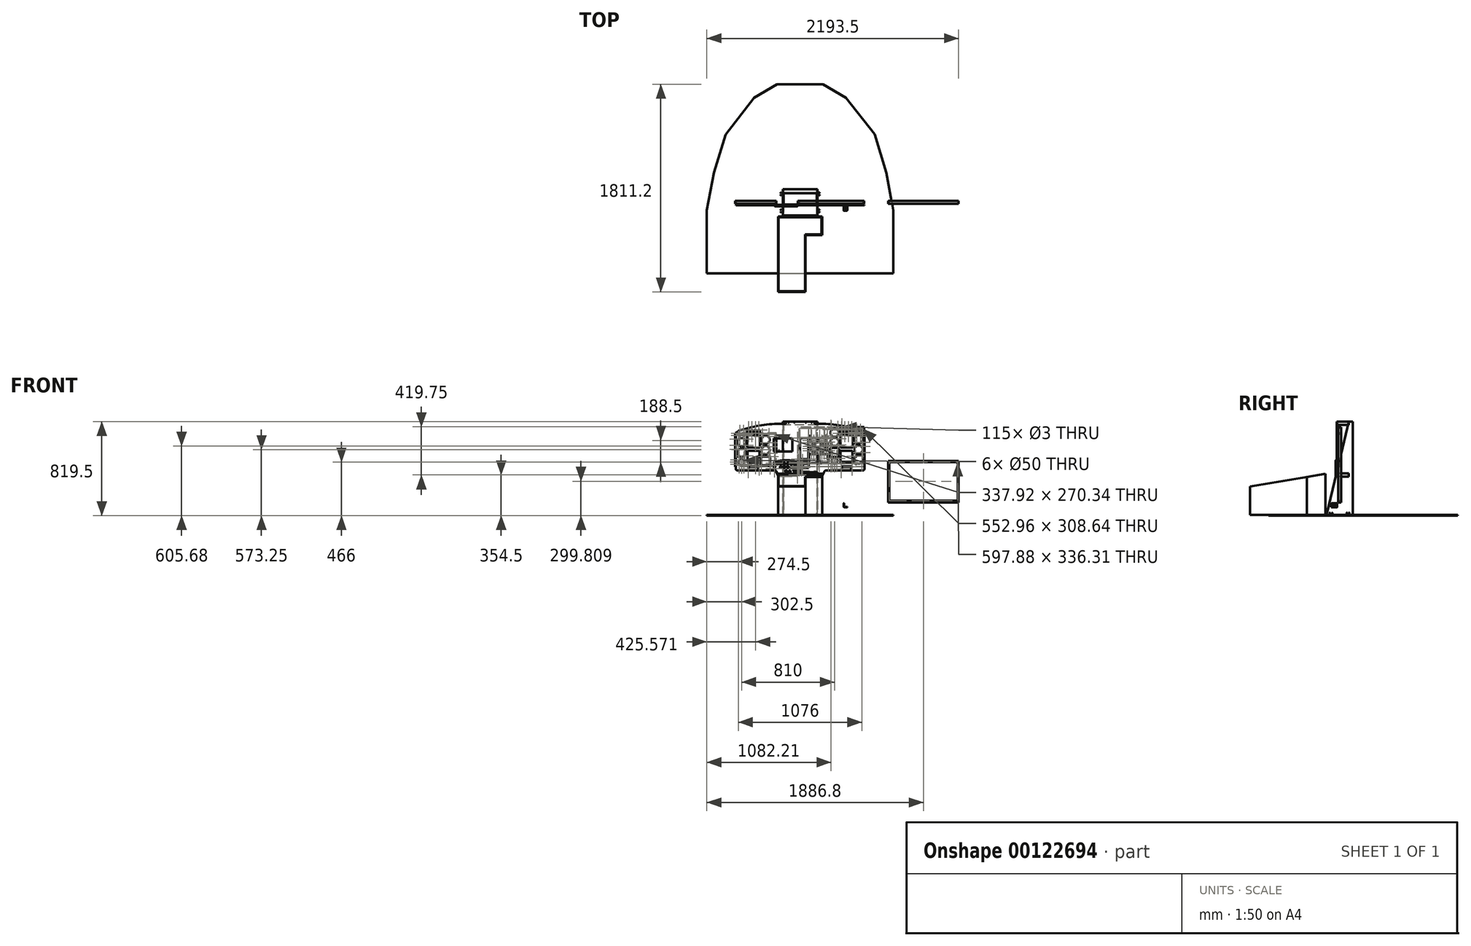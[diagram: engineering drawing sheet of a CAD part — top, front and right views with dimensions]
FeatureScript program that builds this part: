
annotation { "Feature Type Name" : "Feature", "Feature Type Description" : "" }
export const myFeature = defineFeature(function(context is Context, id is Id, definition is map)
    precondition{}
    {
        {
            var Q0;
            Q0=qCreatedBy(makeId("Front.planeOp"),FACE);
            var sketch = newSketch(context, id + "F0", { "sketchPlane" : qUnion([Q0])});
            skLineSegment(sketch, "E0", {"start": v(0, 0) * mm, "end": v(-185, 0) * mm});
            skLineSegment(sketch, "E1", {"start": v(-233, 55.5) * mm, "end": v(-550.5, 55.5) * mm});
            skLineSegment(sketch, "E2", {"start": v(-560, 65) * mm, "end": v(-560, 360) * mm});
            skLineSegment(sketch, "E3", {"start": v(-178, 460) * mm, "end": v(0, 460) * mm});
            skArc(sketch, "E4", {"start": v(-207, 39) * mm, "mid": v(-217.57, 51.08) * mm, "end": v(-233, 55.5) * mm});
            skArc(sketch, "E5", {"start": v(-193, 5.6) * mm, "mid": v(-189.73, 1.76) * mm, "end": v(-185, 0) * mm});
            skLineSegment(sketch, "E6", {"start": v(-207, 39) * mm, "end": v(-193, 5.6) * mm});
            skArc(sketch, "E7", {"start": v(-560, 65) * mm, "mid": v(-557.22, 58.28) * mm, "end": v(-550.5, 55.5) * mm});
            skArc(sketch, "E8", {"start": v(-533, 400) * mm, "mid": v(-552.32, 383.93) * mm, "end": v(-560, 360) * mm});
            skArc(sketch, "E9", {"start": v(-178, 460) * mm, "mid": v(-358.02, 444.9) * mm, "end": v(-533, 400) * mm});
            skArc(sketch, "E10.MirrorCS", {"start": v(193, 5.6) * mm, "mid": v(189.73, 1.76) * mm, "end": v(185, 0) * mm});
            skLineSegment(sketch, "E11.MirrorCS", {"start": v(207, 39) * mm, "end": v(193, 5.6) * mm});
            skArc(sketch, "E12.MirrorCS", {"start": v(560, 65) * mm, "mid": v(557.22, 58.28) * mm, "end": v(550.5, 55.5) * mm});
            skArc(sketch, "E13.MirrorCS", {"start": v(207, 39) * mm, "mid": v(217.57, 51.08) * mm, "end": v(233, 55.5) * mm});
            skArc(sketch, "E14.MirrorCS", {"start": v(533, 400) * mm, "mid": v(552.32, 383.93) * mm, "end": v(560, 360) * mm});
            skArc(sketch, "E15.MirrorCS", {"start": v(178, 460) * mm, "mid": v(358.02, 444.9) * mm, "end": v(533, 400) * mm});
            skLineSegment(sketch, "E16.MirrorCS", {"start": v(178, 460) * mm, "end": v(0, 460) * mm});
            skLineSegment(sketch, "E17.MirrorCS", {"start": v(0, 0) * mm, "end": v(185, 0) * mm});
            skLineSegment(sketch, "E18.MirrorCS", {"start": v(233, 55.5) * mm, "end": v(550.5, 55.5) * mm});
            skLineSegment(sketch, "E19.MirrorCS", {"start": v(560, 65) * mm, "end": v(560, 360) * mm});
            skLineSegment(sketch, "E20.bottom", {"start": v(-125, 460) * mm, "end": v(125, 460) * mm});
            skLineSegment(sketch, "E20.top", {"start": v(-125, 480) * mm, "end": v(125, 480) * mm});
            skLineSegment(sketch, "E20.left", {"start": v(-125, 460) * mm, "end": v(-125, 480) * mm});
            skLineSegment(sketch, "E20.right", {"start": v(125, 460) * mm, "end": v(125, 480) * mm});
            skPoint(sketch, "E20.middle", {"position": v(0, 470) * mm});
            skSolve(sketch);
        }
        {
            var Q0;
            Q0=qSketchRegion(id+"F0",true);
            extrude(context, id + "F1", {"entities" : qUnion([Q0]), "depth" : 3 * mm});
        }
        {
            var Q0;
            Q0=makeQuery(id+"F1.opExtrude","CAP_FACE",FACE,{"disambiguationData":[OSD([sQuery(id+"F0.wireOp",EDGE,"E0"),sQuery(id+"F0.wireOp",EDGE,"E1"),sQuery(id+"F0.wireOp",EDGE,"E2"),sQuery(id+"F0.wireOp",EDGE,"E3"),sQuery(id+"F0.wireOp",EDGE,"E4"),sQuery(id+"F0.wireOp",EDGE,"E5"),sQuery(id+"F0.wireOp",EDGE,"E6"),sQuery(id+"F0.wireOp",EDGE,"E7"),sQuery(id+"F0.wireOp",EDGE,"E8"),sQuery(id+"F0.wireOp",EDGE,"E9"),sQuery(id+"F0.wireOp",EDGE,"E10.MirrorCS"),sQuery(id+"F0.wireOp",EDGE,"E11.MirrorCS"),sQuery(id+"F0.wireOp",EDGE,"E12.MirrorCS"),sQuery(id+"F0.wireOp",EDGE,"E13.MirrorCS"),sQuery(id+"F0.wireOp",EDGE,"E14.MirrorCS"),sQuery(id+"F0.wireOp",EDGE,"E15.MirrorCS"),sQuery(id+"F0.wireOp",EDGE,"E16.MirrorCS"),sQuery(id+"F0.wireOp",EDGE,"E17.MirrorCS"),sQuery(id+"F0.wireOp",EDGE,"E18.MirrorCS"),sQuery(id+"F0.wireOp",EDGE,"E19.MirrorCS")])],"isStart":false});
            var sketch = newSketch(context, id + "F2", { "sketchPlane" : qUnion([Q0])});
            skCircle(sketch, "E21", {"center": v(-510, 300) * mm, "radius": 35 * mm});
            skCircle(sketch, "E22", {"center": v(-510, 210) * mm, "radius": 35 * mm});
            skCircle(sketch, "E23", {"center": v(-510, 126.5) * mm, "radius": 25 * mm});
            skCircle(sketch, "E24", {"center": v(-300, 322) * mm, "radius": 35 * mm});
            skCircle(sketch, "E25", {"center": v(-300, 232) * mm, "radius": 35 * mm});
            skCircle(sketch, "E26", {"center": v(510, 237) * mm, "radius": 35 * mm});
            skCircle(sketch, "E27", {"center": v(510, 325) * mm, "radius": 35 * mm});
            skCircle(sketch, "E28", {"center": v(-538, 328) * mm, "radius": 1.5 * mm});
            skCircle(sketch, "E29", {"center": v(-538, 272) * mm, "radius": 1.5 * mm});
            skCircle(sketch, "E30", {"center": v(-482, 328) * mm, "radius": 1.5 * mm});
            skCircle(sketch, "E31", {"center": v(-482, 272) * mm, "radius": 1.5 * mm});
            skCircle(sketch, "E32", {"center": v(-538, 238) * mm, "radius": 1.5 * mm});
            skCircle(sketch, "E33", {"center": v(-538, 182) * mm, "radius": 1.5 * mm});
            skCircle(sketch, "E34", {"center": v(-482, 238) * mm, "radius": 1.5 * mm});
            skCircle(sketch, "E35", {"center": v(-482, 182) * mm, "radius": 1.5 * mm});
            skCircle(sketch, "E36", {"center": v(-328, 350) * mm, "radius": 1.5 * mm});
            skCircle(sketch, "E37", {"center": v(-272, 350) * mm, "radius": 1.5 * mm});
            skCircle(sketch, "E38", {"center": v(-272, 294) * mm, "radius": 1.5 * mm});
            skCircle(sketch, "E39", {"center": v(-328, 260) * mm, "radius": 1.5 * mm});
            skCircle(sketch, "E40", {"center": v(-272, 260) * mm, "radius": 1.5 * mm});
            skCircle(sketch, "E41", {"center": v(-272, 204) * mm, "radius": 1.5 * mm});
            skLineSegment(sketch, "E42.bottom", {"start": v(-350, 252.75) * mm, "end": v(-460, 252.75) * mm});
            skLineSegment(sketch, "E42.top", {"start": v(-350, 362.75) * mm, "end": v(-460, 362.75) * mm});
            skLineSegment(sketch, "E42.left", {"start": v(-350, 252.75) * mm, "end": v(-350, 362.75) * mm});
            skLineSegment(sketch, "E42.right", {"start": v(-460, 252.75) * mm, "end": v(-460, 362.75) * mm});
            skPoint(sketch, "E42.middle", {"position": v(-405, 307.75) * mm});
            skLineSegment(sketch, "E43.bottom", {"start": v(-352.5, 121) * mm, "end": v(-457.5, 121) * mm});
            skLineSegment(sketch, "E43.top", {"start": v(-352.5, 226) * mm, "end": v(-457.5, 226) * mm});
            skLineSegment(sketch, "E43.left", {"start": v(-352.5, 121) * mm, "end": v(-352.5, 226) * mm});
            skLineSegment(sketch, "E43.right", {"start": v(-457.5, 121) * mm, "end": v(-457.5, 226) * mm});
            skPoint(sketch, "E43.middle", {"position": v(-405, 173.5) * mm});
            skCircle(sketch, "E44", {"center": v(-530, 146.5) * mm, "radius": 1.5 * mm});
            skCircle(sketch, "E45", {"center": v(-530, 106.5) * mm, "radius": 1.5 * mm});
            skCircle(sketch, "E46", {"center": v(-490, 146.5) * mm, "radius": 1.5 * mm});
            skCircle(sketch, "E47", {"center": v(-490, 106.5) * mm, "radius": 1.5 * mm});
            skLineSegment(sketch, "E48.bottom", {"start": v(-362.5, 61.5) * mm, "end": v(-447.5, 61.5) * mm});
            skLineSegment(sketch, "E48.top", {"start": v(-362.5, 89.5) * mm, "end": v(-447.5, 89.5) * mm});
            skLineSegment(sketch, "E48.left", {"start": v(-362.5, 61.5) * mm, "end": v(-362.5, 89.5) * mm});
            skLineSegment(sketch, "E48.right", {"start": v(-447.5, 61.5) * mm, "end": v(-447.5, 89.5) * mm});
            skPoint(sketch, "E48.middle", {"position": v(-405, 75.5) * mm});
            skCircle(sketch, "E49", {"center": v(510, 149) * mm, "radius": 35 * mm});
            skCircle(sketch, "E50", {"center": v(300, 383) * mm, "radius": 35 * mm});
            skCircle(sketch, "E51", {"center": v(300, 303) * mm, "radius": 35 * mm});
            skCircle(sketch, "E52", {"center": v(300, 138) * mm, "radius": 25 * mm});
            skLineSegment(sketch, "E53.0", {"start": v(-260, 165.5) * mm, "end": v(-260, 105.5) * mm});
            skLineSegment(sketch, "E53.1", {"start": v(-260, 105.5) * mm, "end": v(-270, 95.5) * mm});
            skLineSegment(sketch, "E53.2", {"start": v(-270, 95.5) * mm, "end": v(-330, 95.5) * mm});
            skLineSegment(sketch, "E53.3", {"start": v(-330, 95.5) * mm, "end": v(-340, 105.5) * mm});
            skLineSegment(sketch, "E53.4", {"start": v(-340, 105.5) * mm, "end": v(-340, 165.5) * mm});
            skLineSegment(sketch, "E53.5", {"start": v(-340, 165.5) * mm, "end": v(-330, 175.5) * mm});
            skLineSegment(sketch, "E53.6", {"start": v(-330, 175.5) * mm, "end": v(-270, 175.5) * mm});
            skLineSegment(sketch, "E53.7", {"start": v(-270, 175.5) * mm, "end": v(-260, 165.5) * mm});
            skPoint(sketch, "E54", {"position": v(-300, 135.5) * mm});
            skLineSegment(sketch, "E55.bottom", {"start": v(350, 362.75) * mm, "end": v(460, 362.75) * mm});
            skLineSegment(sketch, "E55.top", {"start": v(350, 252.75) * mm, "end": v(460, 252.75) * mm});
            skLineSegment(sketch, "E55.left", {"start": v(350, 362.75) * mm, "end": v(350, 252.75) * mm});
            skLineSegment(sketch, "E55.right", {"start": v(460, 362.75) * mm, "end": v(460, 252.75) * mm});
            skPoint(sketch, "E55.middle", {"position": v(405, 307.75) * mm});
            skLineSegment(sketch, "E56.bottom", {"start": v(352.5, 226) * mm, "end": v(457.5, 226) * mm});
            skLineSegment(sketch, "E56.top", {"start": v(352.5, 121) * mm, "end": v(457.5, 121) * mm});
            skLineSegment(sketch, "E56.left", {"start": v(352.5, 226) * mm, "end": v(352.5, 121) * mm});
            skLineSegment(sketch, "E56.right", {"start": v(457.5, 226) * mm, "end": v(457.5, 121) * mm});
            skPoint(sketch, "E56.middle", {"position": v(405, 173.5) * mm});
            skLineSegment(sketch, "E57.bottom", {"start": v(362.5, 89.5) * mm, "end": v(447.5, 89.5) * mm});
            skLineSegment(sketch, "E57.top", {"start": v(362.5, 61.5) * mm, "end": v(447.5, 61.5) * mm});
            skLineSegment(sketch, "E57.left", {"start": v(362.5, 89.5) * mm, "end": v(362.5, 61.5) * mm});
            skLineSegment(sketch, "E57.right", {"start": v(447.5, 89.5) * mm, "end": v(447.5, 61.5) * mm});
            skPoint(sketch, "E57.middle", {"position": v(405, 75.5) * mm});
            skCircle(sketch, "E58", {"center": v(272, 411) * mm, "radius": 1.5 * mm});
            skCircle(sketch, "E59", {"center": v(272, 355) * mm, "radius": 1.5 * mm});
            skCircle(sketch, "E60", {"center": v(328, 411) * mm, "radius": 1.5 * mm});
            skCircle(sketch, "E61", {"center": v(328, 355) * mm, "radius": 1.5 * mm});
            skCircle(sketch, "E62", {"center": v(272, 331) * mm, "radius": 1.5 * mm});
            skCircle(sketch, "E63", {"center": v(272, 275) * mm, "radius": 1.5 * mm});
            skCircle(sketch, "E64", {"center": v(328, 331) * mm, "radius": 1.5 * mm});
            skCircle(sketch, "E65", {"center": v(328, 275) * mm, "radius": 1.5 * mm});
            skCircle(sketch, "E66", {"center": v(482, 353) * mm, "radius": 1.5 * mm});
            skCircle(sketch, "E67", {"center": v(538, 353) * mm, "radius": 1.5 * mm});
            skCircle(sketch, "E68", {"center": v(538, 297) * mm, "radius": 1.5 * mm});
            skCircle(sketch, "E69", {"center": v(482, 265) * mm, "radius": 1.5 * mm});
            skCircle(sketch, "E70", {"center": v(538, 265) * mm, "radius": 1.5 * mm});
            skCircle(sketch, "E71", {"center": v(538, 209) * mm, "radius": 1.5 * mm});
            skCircle(sketch, "E72", {"center": v(482, 177) * mm, "radius": 1.5 * mm});
            skCircle(sketch, "E73", {"center": v(538, 121) * mm, "radius": 1.5 * mm});
            skCircle(sketch, "E74", {"center": v(280, 158) * mm, "radius": 1.5 * mm});
            skCircle(sketch, "E75", {"center": v(280, 118) * mm, "radius": 1.5 * mm});
            skCircle(sketch, "E76", {"center": v(320, 158) * mm, "radius": 1.5 * mm});
            skCircle(sketch, "E77", {"center": v(320, 118) * mm, "radius": 1.5 * mm});
            skCircle(sketch, "E78", {"center": v(120, 315) * mm, "radius": 25 * mm});
            skCircle(sketch, "E79", {"center": v(100, 335) * mm, "radius": 1.5 * mm});
            skCircle(sketch, "E80", {"center": v(100, 295) * mm, "radius": 1.5 * mm});
            skCircle(sketch, "E81", {"center": v(140, 335) * mm, "radius": 1.5 * mm});
            skCircle(sketch, "E82", {"center": v(140, 295) * mm, "radius": 1.5 * mm});
            skCircle(sketch, "E83", {"center": v(190, 315) * mm, "radius": 25 * mm});
            skCircle(sketch, "E84", {"center": v(170, 335) * mm, "radius": 1.5 * mm});
            skCircle(sketch, "E85", {"center": v(170, 295) * mm, "radius": 1.5 * mm});
            skCircle(sketch, "E86", {"center": v(210, 335) * mm, "radius": 1.5 * mm});
            skCircle(sketch, "E87", {"center": v(210, 295) * mm, "radius": 1.5 * mm});
            skCircle(sketch, "E88", {"center": v(120, 245) * mm, "radius": 25 * mm});
            skCircle(sketch, "E89", {"center": v(100, 265) * mm, "radius": 1.5 * mm});
            skCircle(sketch, "E90", {"center": v(100, 225) * mm, "radius": 1.5 * mm});
            skCircle(sketch, "E91", {"center": v(140, 265) * mm, "radius": 1.5 * mm});
            skCircle(sketch, "E92", {"center": v(140, 225) * mm, "radius": 1.5 * mm});
            skCircle(sketch, "E93", {"center": v(190, 245) * mm, "radius": 25 * mm});
            skCircle(sketch, "E94", {"center": v(170, 265) * mm, "radius": 1.5 * mm});
            skCircle(sketch, "E95", {"center": v(170, 225) * mm, "radius": 1.5 * mm});
            skCircle(sketch, "E96", {"center": v(210, 265) * mm, "radius": 1.5 * mm});
            skCircle(sketch, "E97", {"center": v(210, 225) * mm, "radius": 1.5 * mm});
            skLineSegment(sketch, "E98.0", {"start": v(247.4, 187.54) * mm, "end": v(247.4, 127.54) * mm});
            skLineSegment(sketch, "E98.1", {"start": v(247.4, 127.54) * mm, "end": v(237.4, 117.54) * mm});
            skLineSegment(sketch, "E98.2", {"start": v(237.4, 117.54) * mm, "end": v(177.4, 117.54) * mm});
            skLineSegment(sketch, "E98.3", {"start": v(177.4, 117.54) * mm, "end": v(167.4, 127.54) * mm});
            skLineSegment(sketch, "E98.4", {"start": v(167.4, 127.54) * mm, "end": v(167.4, 187.54) * mm});
            skLineSegment(sketch, "E98.5", {"start": v(167.4, 187.54) * mm, "end": v(177.4, 197.54) * mm});
            skLineSegment(sketch, "E98.6", {"start": v(177.4, 197.54) * mm, "end": v(237.4, 197.54) * mm});
            skLineSegment(sketch, "E98.7", {"start": v(237.4, 197.54) * mm, "end": v(247.4, 187.54) * mm});
            skPoint(sketch, "E99", {"position": v(207.4, 157.54) * mm});
            skLineSegment(sketch, "E100.bottom", {"start": v(55.75, 151.15) * mm, "end": v(12.75, 151.15) * mm});
            skLineSegment(sketch, "E100.top", {"start": v(55.75, 336.15) * mm, "end": v(12.75, 336.15) * mm});
            skLineSegment(sketch, "E100.left", {"start": v(70.75, 166.15) * mm, "end": v(70.75, 321.15) * mm});
            skLineSegment(sketch, "E100.right", {"start": v(-2.25, 166.15) * mm, "end": v(-2.25, 321.15) * mm});
            skPoint(sketch, "E100.middle", {"position": v(34.25, 243.65) * mm});
            skLineSegment(sketch, "E101.bottom", {"start": v(157.52, 116.13) * mm, "end": v(77.52, 116.13) * mm});
            skLineSegment(sketch, "E101.top", {"start": v(157.52, 196.13) * mm, "end": v(77.52, 196.13) * mm});
            skLineSegment(sketch, "E101.left", {"start": v(157.52, 116.13) * mm, "end": v(157.52, 196.13) * mm});
            skLineSegment(sketch, "E101.right", {"start": v(77.52, 116.13) * mm, "end": v(77.52, 196.13) * mm});
            skPoint(sketch, "E101.middle", {"position": v(117.52, 156.13) * mm});
            skLineSegment(sketch, "E102.bottom", {"start": v(-67.27, 218.06) * mm, "end": v(-230.1, 218.06) * mm});
            skLineSegment(sketch, "E102.top", {"start": v(-67.27, 333.61) * mm, "end": v(-230.1, 333.61) * mm});
            skLineSegment(sketch, "E102.left", {"start": v(-67.27, 218.06) * mm, "end": v(-67.27, 333.61) * mm});
            skLineSegment(sketch, "E102.right", {"start": v(-230.1, 218.06) * mm, "end": v(-230.1, 333.61) * mm});
            skPoint(sketch, "E102.middle", {"position": v(-148.69, 275.84) * mm});
            skLineSegment(sketch, "E103.bottom", {"start": v(74.5, 132.23) * mm, "end": v(23.5, 132.23) * mm});
            skLineSegment(sketch, "E103.top", {"start": v(74.5, 76.23) * mm, "end": v(23.5, 76.23) * mm});
            skLineSegment(sketch, "E103.left", {"start": v(23.5, 76.23) * mm, "end": v(23.5, 132.23) * mm});
            skLineSegment(sketch, "E103.right", {"start": v(74.5, 76.23) * mm, "end": v(74.5, 132.23) * mm});
            skPoint(sketch, "E103.middle", {"position": v(49, 104.23) * mm});
            skLineSegment(sketch, "E104.bottom", {"start": v(-350, 402.75) * mm, "end": v(-370, 402.75) * mm});
            skLineSegment(sketch, "E104.top", {"start": v(-350, 382.75) * mm, "end": v(-370, 382.75) * mm});
            skLineSegment(sketch, "E104.left", {"start": v(-350, 402.75) * mm, "end": v(-350, 382.75) * mm});
            skLineSegment(sketch, "E104.right", {"start": v(-370, 402.75) * mm, "end": v(-370, 382.75) * mm});
            skPoint(sketch, "E104.middle", {"position": v(-360, 392.75) * mm});
            skLineSegment(sketch, "E105.bottom", {"start": v(-380, 402.75) * mm, "end": v(-400, 402.75) * mm});
            skLineSegment(sketch, "E105.top", {"start": v(-380, 382.75) * mm, "end": v(-400, 382.75) * mm});
            skLineSegment(sketch, "E105.left", {"start": v(-380, 402.75) * mm, "end": v(-380, 382.75) * mm});
            skLineSegment(sketch, "E105.right", {"start": v(-400, 402.75) * mm, "end": v(-400, 382.75) * mm});
            skPoint(sketch, "E105.middle", {"position": v(-390, 392.75) * mm});
            skLineSegment(sketch, "E106.bottom", {"start": v(-410, 402.75) * mm, "end": v(-430, 402.75) * mm});
            skLineSegment(sketch, "E106.top", {"start": v(-410, 382.75) * mm, "end": v(-430, 382.75) * mm});
            skLineSegment(sketch, "E106.left", {"start": v(-410, 402.75) * mm, "end": v(-410, 382.75) * mm});
            skLineSegment(sketch, "E106.right", {"start": v(-430, 402.75) * mm, "end": v(-430, 382.75) * mm});
            skPoint(sketch, "E106.middle", {"position": v(-420, 392.75) * mm});
            skLineSegment(sketch, "E107.bottom", {"start": v(-440, 402.75) * mm, "end": v(-460, 402.75) * mm});
            skLineSegment(sketch, "E107.top", {"start": v(-440, 382.75) * mm, "end": v(-460, 382.75) * mm});
            skLineSegment(sketch, "E107.left", {"start": v(-440, 402.75) * mm, "end": v(-440, 382.75) * mm});
            skLineSegment(sketch, "E107.right", {"start": v(-460, 402.75) * mm, "end": v(-460, 382.75) * mm});
            skPoint(sketch, "E107.middle", {"position": v(-450, 392.75) * mm});
            skLineSegment(sketch, "E108.bottom", {"start": v(-512.5, 362.75) * mm, "end": v(-539.5, 362.75) * mm});
            skLineSegment(sketch, "E108.top", {"start": v(-512.5, 372.75) * mm, "end": v(-539.5, 372.75) * mm});
            skLineSegment(sketch, "E108.left", {"start": v(-512.5, 362.75) * mm, "end": v(-512.5, 372.75) * mm});
            skLineSegment(sketch, "E108.right", {"start": v(-539.5, 362.75) * mm, "end": v(-539.5, 372.75) * mm});
            skPoint(sketch, "E108.middle", {"position": v(-526, 367.75) * mm});
            skLineSegment(sketch, "E109.bottom", {"start": v(-480.5, 362.75) * mm, "end": v(-507.5, 362.75) * mm});
            skLineSegment(sketch, "E109.top", {"start": v(-480.5, 372.75) * mm, "end": v(-507.5, 372.75) * mm});
            skLineSegment(sketch, "E109.left", {"start": v(-480.5, 362.75) * mm, "end": v(-480.5, 372.75) * mm});
            skLineSegment(sketch, "E109.right", {"start": v(-507.5, 362.75) * mm, "end": v(-507.5, 372.75) * mm});
            skPoint(sketch, "E109.middle", {"position": v(-494, 367.75) * mm});
            skPoint(sketch, "E110.middle", {"position": v(231.43, 263.64) * mm});
            skPoint(sketch, "E111.visualSharp", {"position": v(-2.25, 336.15) * mm});
            skArc(sketch, "E111.filletArc", {"start": v(12.75, 336.15) * mm, "mid": v(2.14, 331.76) * mm, "end": v(-2.25, 321.15) * mm});
            skPoint(sketch, "E112.visualSharp", {"position": v(70.75, 336.15) * mm});
            skArc(sketch, "E112.filletArc", {"start": v(70.75, 321.15) * mm, "mid": v(66.35, 331.76) * mm, "end": v(55.75, 336.15) * mm});
            skPoint(sketch, "E113.visualSharp", {"position": v(-2.25, 151.15) * mm});
            skArc(sketch, "E113.filletArc", {"start": v(-2.25, 166.15) * mm, "mid": v(2.14, 155.54) * mm, "end": v(12.75, 151.15) * mm});
            skPoint(sketch, "E114.visualSharp", {"position": v(70.75, 151.15) * mm});
            skArc(sketch, "E114.filletArc", {"start": v(55.75, 151.15) * mm, "mid": v(66.35, 155.54) * mm, "end": v(70.75, 166.15) * mm});
            skLineSegment(sketch, "E115.bottom", {"start": v(460, 402.75) * mm, "end": v(440, 402.75) * mm});
            skLineSegment(sketch, "E115.top", {"start": v(460, 382.75) * mm, "end": v(440, 382.75) * mm});
            skLineSegment(sketch, "E115.left", {"start": v(460, 402.75) * mm, "end": v(460, 382.75) * mm});
            skLineSegment(sketch, "E115.right", {"start": v(440, 402.75) * mm, "end": v(440, 382.75) * mm});
            skPoint(sketch, "E115.middle", {"position": v(450, 392.75) * mm});
            skLineSegment(sketch, "E116.bottom", {"start": v(430, 402.75) * mm, "end": v(410, 402.75) * mm});
            skLineSegment(sketch, "E116.top", {"start": v(430, 382.75) * mm, "end": v(410, 382.75) * mm});
            skLineSegment(sketch, "E116.left", {"start": v(430, 402.75) * mm, "end": v(430, 382.75) * mm});
            skLineSegment(sketch, "E116.right", {"start": v(410, 402.75) * mm, "end": v(410, 382.75) * mm});
            skPoint(sketch, "E116.middle", {"position": v(420, 392.75) * mm});
            skLineSegment(sketch, "E117.bottom", {"start": v(400, 402.75) * mm, "end": v(380, 402.75) * mm});
            skLineSegment(sketch, "E117.top", {"start": v(400, 382.75) * mm, "end": v(380, 382.75) * mm});
            skLineSegment(sketch, "E117.left", {"start": v(400, 402.75) * mm, "end": v(400, 382.75) * mm});
            skLineSegment(sketch, "E117.right", {"start": v(380, 402.75) * mm, "end": v(380, 382.75) * mm});
            skPoint(sketch, "E117.middle", {"position": v(390, 392.75) * mm});
            skLineSegment(sketch, "E118.bottom", {"start": v(370, 402.75) * mm, "end": v(350, 402.75) * mm});
            skLineSegment(sketch, "E118.top", {"start": v(370, 382.75) * mm, "end": v(350, 382.75) * mm});
            skLineSegment(sketch, "E118.left", {"start": v(370, 402.75) * mm, "end": v(370, 382.75) * mm});
            skLineSegment(sketch, "E118.right", {"start": v(350, 402.75) * mm, "end": v(350, 382.75) * mm});
            skPoint(sketch, "E118.middle", {"position": v(360, 392.75) * mm});
            skLineSegment(sketch, "E119.bottom", {"start": v(507.5, 372.75) * mm, "end": v(480.5, 372.75) * mm});
            skLineSegment(sketch, "E119.top", {"start": v(507.5, 382.75) * mm, "end": v(480.5, 382.75) * mm});
            skLineSegment(sketch, "E119.left", {"start": v(507.5, 372.75) * mm, "end": v(507.5, 382.75) * mm});
            skLineSegment(sketch, "E119.right", {"start": v(480.5, 372.75) * mm, "end": v(480.5, 382.75) * mm});
            skPoint(sketch, "E119.middle", {"position": v(494, 377.75) * mm});
            skLineSegment(sketch, "E120.bottom", {"start": v(539.5, 372.75) * mm, "end": v(512.5, 372.75) * mm});
            skLineSegment(sketch, "E120.top", {"start": v(539.5, 382.75) * mm, "end": v(512.5, 382.75) * mm});
            skLineSegment(sketch, "E120.left", {"start": v(539.5, 372.75) * mm, "end": v(539.5, 382.75) * mm});
            skLineSegment(sketch, "E120.right", {"start": v(512.5, 372.75) * mm, "end": v(512.5, 382.75) * mm});
            skPoint(sketch, "E120.middle", {"position": v(526, 377.75) * mm});
            skLineSegment(sketch, "E121.bottom", {"start": v(377, 419.75) * mm, "end": v(350, 419.75) * mm});
            skLineSegment(sketch, "E121.top", {"start": v(377, 429.75) * mm, "end": v(350, 429.75) * mm});
            skLineSegment(sketch, "E121.left", {"start": v(377, 419.75) * mm, "end": v(377, 429.75) * mm});
            skLineSegment(sketch, "E121.right", {"start": v(350, 429.75) * mm, "end": v(350, 419.75) * mm});
            skPoint(sketch, "E121.middle", {"position": v(363.5, 424.75) * mm});
            skLineSegment(sketch, "E122.bottom", {"start": v(231.16, 356.5) * mm, "end": v(221.16, 356.5) * mm});
            skLineSegment(sketch, "E122.top", {"start": v(231.16, 329.5) * mm, "end": v(221.16, 329.5) * mm});
            skLineSegment(sketch, "E122.left", {"start": v(231.16, 356.5) * mm, "end": v(231.16, 329.5) * mm});
            skLineSegment(sketch, "E122.right", {"start": v(221.16, 356.5) * mm, "end": v(221.16, 329.5) * mm});
            skPoint(sketch, "E122.middle", {"position": v(226.16, 343) * mm});
            skLineSegment(sketch, "E123.bottom", {"start": v(90.02, 329.5) * mm, "end": v(80.02, 329.5) * mm});
            skLineSegment(sketch, "E123.top", {"start": v(90.02, 356.5) * mm, "end": v(80.02, 356.5) * mm});
            skLineSegment(sketch, "E123.left", {"start": v(90.02, 329.5) * mm, "end": v(90.02, 356.5) * mm});
            skLineSegment(sketch, "E123.right", {"start": v(80.02, 329.5) * mm, "end": v(80.02, 356.5) * mm});
            skPoint(sketch, "E123.middle", {"position": v(85.02, 343) * mm});
            skCircle(sketch, "E124", {"center": v(-2.25, 336.15) * mm, "radius": 1.5 * mm});
            skCircle(sketch, "E125", {"center": v(70.75, 336.15) * mm, "radius": 1.5 * mm});
            skCircle(sketch, "E126", {"center": v(-2.25, 151.15) * mm, "radius": 1.5 * mm});
            skCircle(sketch, "E127", {"center": v(70.75, 151.15) * mm, "radius": 1.5 * mm});
            skCircle(sketch, "E128", {"center": v(168.4, 196.54) * mm, "radius": 1.5 * mm});
            skCircle(sketch, "E129", {"center": v(168.4, 118.54) * mm, "radius": 1.5 * mm});
            skCircle(sketch, "E130", {"center": v(246.4, 196.54) * mm, "radius": 1.5 * mm});
            skCircle(sketch, "E131", {"center": v(246.4, 118.54) * mm, "radius": 1.5 * mm});
            skCircle(sketch, "E132", {"center": v(-338.5, 174) * mm, "radius": 1.5 * mm});
            skCircle(sketch, "E133", {"center": v(-338.5, 97) * mm, "radius": 1.5 * mm});
            skCircle(sketch, "E134", {"center": v(-261.5, 174) * mm, "radius": 1.5 * mm});
            skCircle(sketch, "E135", {"center": v(-261.5, 97) * mm, "radius": 1.5 * mm});
            skCircle(sketch, "E136", {"center": v(231.43, 301.14) * mm, "radius": 1.5 * mm});
            skCircle(sketch, "E137", {"center": v(231.43, 226.14) * mm, "radius": 1.5 * mm});
            skLineSegment(sketch, "E138.bottom", {"start": v(241.43, 228.64) * mm, "end": v(221.43, 228.64) * mm});
            skLineSegment(sketch, "E138.top", {"start": v(241.43, 298.64) * mm, "end": v(221.43, 298.64) * mm});
            skLineSegment(sketch, "E138.left", {"start": v(241.43, 228.64) * mm, "end": v(241.43, 298.64) * mm});
            skLineSegment(sketch, "E138.right", {"start": v(221.43, 228.64) * mm, "end": v(221.43, 298.64) * mm});
            skCircle(sketch, "E139", {"center": v(-450, 407.75) * mm, "radius": 1.5 * mm});
            skCircle(sketch, "E140", {"center": v(-450, 377.75) * mm, "radius": 1.5 * mm});
            skCircle(sketch, "E141", {"center": v(-526, 377.75) * mm, "radius": 1.5 * mm});
            skCircle(sketch, "E142", {"center": v(-526, 357.75) * mm, "radius": 1.5 * mm});
            skCircle(sketch, "E143", {"center": v(-494, 377.75) * mm, "radius": 1.5 * mm});
            skCircle(sketch, "E144", {"center": v(-494, 357.75) * mm, "radius": 1.5 * mm});
            skCircle(sketch, "E145", {"center": v(-420, 407.75) * mm, "radius": 1.5 * mm});
            skCircle(sketch, "E146", {"center": v(-420, 377.75) * mm, "radius": 1.5 * mm});
            skCircle(sketch, "E147", {"center": v(-390, 407.75) * mm, "radius": 1.5 * mm});
            skCircle(sketch, "E148", {"center": v(-390, 377.75) * mm, "radius": 1.5 * mm});
            skCircle(sketch, "E149", {"center": v(-360, 407.75) * mm, "radius": 1.5 * mm});
            skCircle(sketch, "E150", {"center": v(-360, 377.75) * mm, "radius": 1.5 * mm});
            skCircle(sketch, "E151", {"center": v(360, 377.75) * mm, "radius": 1.5 * mm});
            skCircle(sketch, "E152", {"center": v(390, 407.75) * mm, "radius": 1.5 * mm});
            skCircle(sketch, "E153", {"center": v(420, 407.75) * mm, "radius": 1.5 * mm});
            skCircle(sketch, "E154", {"center": v(450, 407.75) * mm, "radius": 1.5 * mm});
            skCircle(sketch, "E155", {"center": v(390, 377.75) * mm, "radius": 1.5 * mm});
            skCircle(sketch, "E156", {"center": v(420, 377.75) * mm, "radius": 1.5 * mm});
            skCircle(sketch, "E157", {"center": v(450, 377.75) * mm, "radius": 1.5 * mm});
            skCircle(sketch, "E158", {"center": v(360, 407.75) * mm, "radius": 1.5 * mm});
            skCircle(sketch, "E159", {"center": v(363.5, 434.75) * mm, "radius": 1.5 * mm});
            skCircle(sketch, "E160", {"center": v(363.5, 414.75) * mm, "radius": 1.5 * mm});
            skCircle(sketch, "E161", {"center": v(494, 387.75) * mm, "radius": 1.5 * mm});
            skCircle(sketch, "E162", {"center": v(526, 387.75) * mm, "radius": 1.5 * mm});
            skCircle(sketch, "E163", {"center": v(494, 367.75) * mm, "radius": 1.5 * mm});
            skCircle(sketch, "E164", {"center": v(526, 367.75) * mm, "radius": 1.5 * mm});
            skCircle(sketch, "E165", {"center": v(236.16, 343) * mm, "radius": 1.5 * mm});
            skCircle(sketch, "E166", {"center": v(216.16, 343) * mm, "radius": 1.5 * mm});
            skCircle(sketch, "E167", {"center": v(75.02, 343) * mm, "radius": 1.5 * mm});
            skCircle(sketch, "E168", {"center": v(95.02, 343) * mm, "radius": 1.5 * mm});
            skLineSegment(sketch, "E169", {"start": v(270, 250.7) * mm, "end": v(330, 250.7) * mm});
            skLineSegment(sketch, "E170", {"start": v(330, 250.7) * mm, "end": v(340, 240.7) * mm});
            skLineSegment(sketch, "E171", {"start": v(340, 240.7) * mm, "end": v(340, 180.7) * mm});
            skLineSegment(sketch, "E172", {"start": v(340, 180.7) * mm, "end": v(330, 170.7) * mm});
            skLineSegment(sketch, "E173", {"start": v(330, 170.7) * mm, "end": v(270, 170.7) * mm});
            skLineSegment(sketch, "E174", {"start": v(270, 170.7) * mm, "end": v(260, 180.7) * mm});
            skLineSegment(sketch, "E175", {"start": v(260, 180.7) * mm, "end": v(260, 240.7) * mm});
            skLineSegment(sketch, "E176", {"start": v(260, 240.7) * mm, "end": v(270, 250.7) * mm});
            skCircle(sketch, "E177", {"center": v(261, 249.7) * mm, "radius": 1.5 * mm});
            skCircle(sketch, "E178", {"center": v(339, 249.7) * mm, "radius": 1.5 * mm});
            skCircle(sketch, "E179", {"center": v(261, 171.7) * mm, "radius": 1.5 * mm});
            skCircle(sketch, "E180", {"center": v(339, 172.1) * mm, "radius": 1.5 * mm});
            skPoint(sketch, "E181", {"position": v(300, 210.7) * mm});
            skCircle(sketch, "E182", {"center": v(-223, 119.04) * mm, "radius": 1.5 * mm});
            skCircle(sketch, "E183", {"center": v(-223, 70.77) * mm, "radius": 1.5 * mm});
            skCircle(sketch, "E184", {"center": v(-22, 119.04) * mm, "radius": 1.5 * mm});
            skCircle(sketch, "E185", {"center": v(-22, 67.04) * mm, "radius": 1.5 * mm});
            skCircle(sketch, "E186", {"center": v(-22, 15) * mm, "radius": 1.5 * mm});
            skLineSegment(sketch, "E187", {"start": v(-213, 131) * mm, "end": v(-32, 131) * mm});
            skLineSegment(sketch, "E188", {"start": v(-32, 131) * mm, "end": v(-32, 13) * mm});
            skLineSegment(sketch, "E189", {"start": v(-32, 13) * mm, "end": v(-181.54, 13) * mm});
            skLineSegment(sketch, "E190", {"start": v(-181.54, 13) * mm, "end": v(-213, 63) * mm});
            skLineSegment(sketch, "E191", {"start": v(-213, 63) * mm, "end": v(-213, 131) * mm});
            skCircle(sketch, "E192", {"center": v(2.83, 105.5) * mm, "radius": 18.5 * mm});
            skCircle(sketch, "E193", {"center": v(19.83, 122.5) * mm, "radius": 1.5 * mm});
            skCircle(sketch, "E194", {"center": v(-14.17, 122.5) * mm, "radius": 1.5 * mm});
            skCircle(sketch, "E195", {"center": v(-14.17, 88.5) * mm, "radius": 1.5 * mm});
            skCircle(sketch, "E196", {"center": v(19.83, 88.5) * mm, "radius": 1.5 * mm});
            skLineSegment(sketch, "E197.bottom", {"start": v(5.9, 43.8) * mm, "end": v(-0.23, 43.8) * mm});
            skLineSegment(sketch, "E197.top", {"start": v(5.9, 65.57) * mm, "end": v(-0.23, 65.57) * mm});
            skLineSegment(sketch, "E197.left", {"start": v(5.9, 43.8) * mm, "end": v(5.9, 65.57) * mm});
            skLineSegment(sketch, "E197.right", {"start": v(-0.23, 43.8) * mm, "end": v(-0.23, 65.57) * mm});
            skPoint(sketch, "E197.middle", {"position": v(2.83, 54.68) * mm});
            skCircle(sketch, "E198", {"center": v(-7.17, 79.68) * mm, "radius": 1.5 * mm});
            skCircle(sketch, "E199", {"center": v(12.83, 79.68) * mm, "radius": 1.5 * mm});
            skCircle(sketch, "E200", {"center": v(-452.5, 65.5) * mm, "radius": 1.5 * mm});
            skCircle(sketch, "E201", {"center": v(-357.5, 85.5) * mm, "radius": 1.5 * mm});
            skCircle(sketch, "E202", {"center": v(452.5, 85.5) * mm, "radius": 1.5 * mm});
            skCircle(sketch, "E203", {"center": v(357.5, 65.5) * mm, "radius": 1.5 * mm});
            skSolve(sketch);
        }
        {
            var Q0;
            Q0=sQuery(id+"F2.wireOp",VERTEX,"E21.center");
            var Q1;
            Q1=sQuery(id+"F2.wireOp",VERTEX,"E24.center");
            var Q2;
            Q2=sQuery(id+"F2.wireOp",VERTEX,"E25.center");
            var Q3;
            Q3=sQuery(id+"F2.wireOp",VERTEX,"E22.center");
            var Q4;
            Q4=sQuery(id+"F2.wireOp",VERTEX,"E50.center");
            var Q5;
            Q5=sQuery(id+"F2.wireOp",VERTEX,"E51.center");
            var Q6;
            Q6=sQuery(id+"F2.wireOp",VERTEX,"E26.center");
            var Q7;
            Q7=sQuery(id+"F2.wireOp",VERTEX,"E27.center");
            var Q8;
            Q8=sQuery(id+"F2.wireOp",VERTEX,"E49.center");
            var Q9;
            Q9=makeQuery(id+"F1.opExtrude","SWEPT_BODY",BODY,{"disambiguationData":[OSD([sQuery(id+"F0.wireOp",EDGE,"E0"),sQuery(id+"F0.wireOp",EDGE,"E1"),sQuery(id+"F0.wireOp",EDGE,"E2"),sQuery(id+"F0.wireOp",EDGE,"E3"),sQuery(id+"F0.wireOp",EDGE,"E4"),sQuery(id+"F0.wireOp",EDGE,"E5"),sQuery(id+"F0.wireOp",EDGE,"E6"),sQuery(id+"F0.wireOp",EDGE,"E7"),sQuery(id+"F0.wireOp",EDGE,"E8"),sQuery(id+"F0.wireOp",EDGE,"E9"),sQuery(id+"F0.wireOp",EDGE,"E10.MirrorCS"),sQuery(id+"F0.wireOp",EDGE,"E11.MirrorCS"),sQuery(id+"F0.wireOp",EDGE,"E12.MirrorCS"),sQuery(id+"F0.wireOp",EDGE,"E13.MirrorCS"),sQuery(id+"F0.wireOp",EDGE,"E14.MirrorCS"),sQuery(id+"F0.wireOp",EDGE,"E15.MirrorCS"),sQuery(id+"F0.wireOp",EDGE,"E16.MirrorCS"),sQuery(id+"F0.wireOp",EDGE,"E17.MirrorCS"),sQuery(id+"F0.wireOp",EDGE,"E18.MirrorCS"),sQuery(id+"F0.wireOp",EDGE,"E19.MirrorCS")])]});
            hole(context, id + "F3", {"style" : HoleStyle.SIMPLE, "endStyle" : HoleEndStyle.THROUGH, "holeDiameter" : 70 * mm, "locations" : qUnion([Q0, Q1, Q2, Q3, Q4, Q5, Q6, Q7, Q8]), "scope" : qUnion([Q9]), "isTappedThrough" : true});
        }
        {
            var Q0;
            Q0=sQuery(id+"F2.wireOp",VERTEX,"E23.center");
            var Q1;
            Q1=sQuery(id+"F2.wireOp",VERTEX,"E52.center");
            var Q2;
            Q2=sQuery(id+"F2.wireOp",VERTEX,"E78.center");
            var Q3;
            Q3=sQuery(id+"F2.wireOp",VERTEX,"E83.center");
            var Q4;
            Q4=sQuery(id+"F2.wireOp",VERTEX,"E93.center");
            var Q5;
            Q5=sQuery(id+"F2.wireOp",VERTEX,"E88.center");
            var Q6;
            Q6=makeQuery(id+"F1.opExtrude","SWEPT_BODY",BODY,{"disambiguationData":[OSD([sQuery(id+"F0.wireOp",EDGE,"E0"),sQuery(id+"F0.wireOp",EDGE,"E1"),sQuery(id+"F0.wireOp",EDGE,"E2"),sQuery(id+"F0.wireOp",EDGE,"E3"),sQuery(id+"F0.wireOp",EDGE,"E4"),sQuery(id+"F0.wireOp",EDGE,"E5"),sQuery(id+"F0.wireOp",EDGE,"E6"),sQuery(id+"F0.wireOp",EDGE,"E7"),sQuery(id+"F0.wireOp",EDGE,"E8"),sQuery(id+"F0.wireOp",EDGE,"E9"),sQuery(id+"F0.wireOp",EDGE,"E10.MirrorCS"),sQuery(id+"F0.wireOp",EDGE,"E11.MirrorCS"),sQuery(id+"F0.wireOp",EDGE,"E12.MirrorCS"),sQuery(id+"F0.wireOp",EDGE,"E13.MirrorCS"),sQuery(id+"F0.wireOp",EDGE,"E14.MirrorCS"),sQuery(id+"F0.wireOp",EDGE,"E15.MirrorCS"),sQuery(id+"F0.wireOp",EDGE,"E16.MirrorCS"),sQuery(id+"F0.wireOp",EDGE,"E17.MirrorCS"),sQuery(id+"F0.wireOp",EDGE,"E18.MirrorCS"),sQuery(id+"F0.wireOp",EDGE,"E19.MirrorCS")])]});
            hole(context, id + "F4", {"style" : HoleStyle.SIMPLE, "endStyle" : HoleEndStyle.THROUGH, "holeDiameter" : 50 * mm, "locations" : qUnion([Q0, Q1, Q2, Q3, Q4, Q5]), "scope" : qUnion([Q6]), "isTappedThrough" : true});
        }
        {
            var Q0;
            Q0=makeQuery(id+"F1.opExtrude","CAP_FACE",FACE,{"disambiguationData":[OSD([sQuery(id+"F0.wireOp",EDGE,"E0"),sQuery(id+"F0.wireOp",EDGE,"E1"),sQuery(id+"F0.wireOp",EDGE,"E2"),sQuery(id+"F0.wireOp",EDGE,"E3"),sQuery(id+"F0.wireOp",EDGE,"E4"),sQuery(id+"F0.wireOp",EDGE,"E5"),sQuery(id+"F0.wireOp",EDGE,"E6"),sQuery(id+"F0.wireOp",EDGE,"E7"),sQuery(id+"F0.wireOp",EDGE,"E8"),sQuery(id+"F0.wireOp",EDGE,"E9"),sQuery(id+"F0.wireOp",EDGE,"E10.MirrorCS"),sQuery(id+"F0.wireOp",EDGE,"E11.MirrorCS"),sQuery(id+"F0.wireOp",EDGE,"E12.MirrorCS"),sQuery(id+"F0.wireOp",EDGE,"E13.MirrorCS"),sQuery(id+"F0.wireOp",EDGE,"E14.MirrorCS"),sQuery(id+"F0.wireOp",EDGE,"E15.MirrorCS"),sQuery(id+"F0.wireOp",EDGE,"E16.MirrorCS"),sQuery(id+"F0.wireOp",EDGE,"E17.MirrorCS"),sQuery(id+"F0.wireOp",EDGE,"E18.MirrorCS"),sQuery(id+"F0.wireOp",EDGE,"E19.MirrorCS")])],"isStart":false});
            var sketch = newSketch(context, id + "F5", { "sketchPlane" : qUnion([Q0])});
            skCircle(sketch, "E204", {"center": v(-50, 473) * mm, "radius": 2.5 * mm});
            skCircle(sketch, "E205", {"center": v(-100, 473) * mm, "radius": 2.5 * mm});
            skCircle(sketch, "E206", {"center": v(-50, 7) * mm, "radius": 2.5 * mm});
            skCircle(sketch, "E207", {"center": v(-100, 7) * mm, "radius": 2.5 * mm});
            skCircle(sketch, "E208.MirrorC", {"center": v(100, 7) * mm, "radius": 2.5 * mm});
            skCircle(sketch, "E209.MirrorC", {"center": v(50, 7) * mm, "radius": 2.5 * mm});
            skCircle(sketch, "E210.MirrorC", {"center": v(100, 473) * mm, "radius": 2.5 * mm});
            skCircle(sketch, "E211.MirrorC", {"center": v(50, 473) * mm, "radius": 2.5 * mm});
            skSolve(sketch);
        }
        {
            var Q0;
            Q0=sQuery(id+"F2.wireOp",VERTEX,"E28.center");
            var Q1;
            Q1=sQuery(id+"F2.wireOp",VERTEX,"E30.center");
            var Q2;
            Q2=sQuery(id+"F2.wireOp",VERTEX,"E29.center");
            var Q3;
            Q3=sQuery(id+"F2.wireOp",VERTEX,"E31.center");
            var Q4;
            Q4=sQuery(id+"F2.wireOp",VERTEX,"a418828e-2c56-4529-a2cb-2e7b7d108326.center");
            var Q5;
            Q5=sQuery(id+"F2.wireOp",VERTEX,"E36.center");
            var Q6;
            Q6=sQuery(id+"F2.wireOp",VERTEX,"E37.center");
            var Q7;
            Q7=sQuery(id+"F2.wireOp",VERTEX,"E38.center");
            var Q8;
            Q8=sQuery(id+"F2.wireOp",VERTEX,"E34.center");
            var Q9;
            Q9=sQuery(id+"F2.wireOp",VERTEX,"E32.center");
            var Q10;
            Q10=sQuery(id+"F2.wireOp",VERTEX,"E35.center");
            var Q11;
            Q11=sQuery(id+"F2.wireOp",VERTEX,"E33.center");
            var Q12;
            Q12=sQuery(id+"F2.wireOp",VERTEX,"E46.center");
            var Q13;
            Q13=sQuery(id+"F2.wireOp",VERTEX,"E44.center");
            var Q14;
            Q14=sQuery(id+"F2.wireOp",VERTEX,"E45.center");
            var Q15;
            Q15=sQuery(id+"F2.wireOp",VERTEX,"E47.center");
            var Q16;
            Q16=sQuery(id+"F2.wireOp",VERTEX,"5f2a77c0-05be-4e49-994f-5ad012f67cbe.center");
            var Q17;
            Q17=sQuery(id+"F2.wireOp",VERTEX,"E41.center");
            var Q18;
            Q18=sQuery(id+"F2.wireOp",VERTEX,"E40.center");
            var Q19;
            Q19=sQuery(id+"F2.wireOp",VERTEX,"E39.center");
            var Q20;
            Q20=sQuery(id+"F2.wireOp",VERTEX,"E58.center");
            var Q21;
            Q21=sQuery(id+"F2.wireOp",VERTEX,"E60.center");
            var Q22;
            Q22=sQuery(id+"F2.wireOp",VERTEX,"E61.center");
            var Q23;
            Q23=sQuery(id+"F2.wireOp",VERTEX,"E59.center");
            var Q24;
            Q24=sQuery(id+"F2.wireOp",VERTEX,"E62.center");
            var Q25;
            Q25=sQuery(id+"F2.wireOp",VERTEX,"E64.center");
            var Q26;
            Q26=sQuery(id+"F2.wireOp",VERTEX,"E65.center");
            var Q27;
            Q27=sQuery(id+"F2.wireOp",VERTEX,"E63.center");
            var Q28;
            Q28=sQuery(id+"F2.wireOp",VERTEX,"E76.center");
            var Q29;
            Q29=sQuery(id+"F2.wireOp",VERTEX,"E74.center");
            var Q30;
            Q30=sQuery(id+"F2.wireOp",VERTEX,"E75.center");
            var Q31;
            Q31=sQuery(id+"F2.wireOp",VERTEX,"E77.center");
            var Q32;
            Q32=sQuery(id+"F2.wireOp",VERTEX,"10ae047a-8e50-4906-9f25-43b7f80e6f66.center");
            var Q33;
            Q33=sQuery(id+"F2.wireOp",VERTEX,"E73.center");
            var Q34;
            Q34=sQuery(id+"F2.wireOp",VERTEX,"a88b3004-4fcf-449b-872c-055799e025b4.center");
            var Q35;
            Q35=sQuery(id+"F2.wireOp",VERTEX,"E72.center");
            var Q36;
            Q36=sQuery(id+"F2.wireOp",VERTEX,"6e882f2b-3fe4-47b6-9df0-26abe4f9f71a.center");
            var Q37;
            Q37=sQuery(id+"F2.wireOp",VERTEX,"E71.center");
            var Q38;
            Q38=sQuery(id+"F2.wireOp",VERTEX,"E70.center");
            var Q39;
            Q39=sQuery(id+"F2.wireOp",VERTEX,"E69.center");
            var Q40;
            Q40=sQuery(id+"F2.wireOp",VERTEX,"E68.center");
            var Q41;
            Q41=sQuery(id+"F2.wireOp",VERTEX,"2e8b786a-5f49-48c3-a018-00c32246a49a.center");
            var Q42;
            Q42=sQuery(id+"F2.wireOp",VERTEX,"E66.center");
            var Q43;
            Q43=sQuery(id+"F2.wireOp",VERTEX,"E67.center");
            var Q44;
            Q44=sQuery(id+"F2.wireOp",VERTEX,"E79.center");
            var Q45;
            Q45=sQuery(id+"F2.wireOp",VERTEX,"E81.center");
            var Q46;
            Q46=sQuery(id+"F2.wireOp",VERTEX,"E82.center");
            var Q47;
            Q47=sQuery(id+"F2.wireOp",VERTEX,"E80.center");
            var Q48;
            Q48=sQuery(id+"F2.wireOp",VERTEX,"E84.center");
            var Q49;
            Q49=sQuery(id+"F2.wireOp",VERTEX,"E85.center");
            var Q50;
            Q50=sQuery(id+"F2.wireOp",VERTEX,"E87.center");
            var Q51;
            Q51=sQuery(id+"F2.wireOp",VERTEX,"E86.center");
            var Q52;
            Q52=sQuery(id+"F2.wireOp",VERTEX,"E89.center");
            var Q53;
            Q53=sQuery(id+"F2.wireOp",VERTEX,"E90.center");
            var Q54;
            Q54=sQuery(id+"F2.wireOp",VERTEX,"E92.center");
            var Q55;
            Q55=sQuery(id+"F2.wireOp",VERTEX,"E91.center");
            var Q56;
            Q56=sQuery(id+"F2.wireOp",VERTEX,"E94.center");
            var Q57;
            Q57=sQuery(id+"F2.wireOp",VERTEX,"E95.center");
            var Q58;
            Q58=sQuery(id+"F2.wireOp",VERTEX,"E97.center");
            var Q59;
            Q59=sQuery(id+"F2.wireOp",VERTEX,"E96.center");
            var Q60;
            Q60=sQuery(id+"F2.wireOp",VERTEX,"E112.visualSharp");
            var Q61;
            Q61=sQuery(id+"F2.wireOp",VERTEX,"E111.visualSharp");
            var Q62;
            Q62=sQuery(id+"F2.wireOp",VERTEX,"E114.visualSharp");
            var Q63;
            Q63=sQuery(id+"F2.wireOp",VERTEX,"E113.visualSharp");
            var Q64;
            Q64=sQuery(id+"F2.wireOp",VERTEX,"E134.center");
            var Q65;
            Q65=sQuery(id+"F2.wireOp",VERTEX,"E132.center");
            var Q66;
            Q66=sQuery(id+"F2.wireOp",VERTEX,"E133.center");
            var Q67;
            Q67=sQuery(id+"F2.wireOp",VERTEX,"E135.center");
            var Q68;
            Q68=sQuery(id+"F2.wireOp",VERTEX,"E128.center");
            var Q69;
            Q69=sQuery(id+"F2.wireOp",VERTEX,"E130.center");
            var Q70;
            Q70=sQuery(id+"F2.wireOp",VERTEX,"E131.center");
            var Q71;
            Q71=sQuery(id+"F2.wireOp",VERTEX,"E129.center");
            var Q72;
            Q72=sQuery(id+"F2.wireOp",VERTEX,"E136.center");
            var Q73;
            Q73=sQuery(id+"F2.wireOp",VERTEX,"E137.center");
            var Q74;
            Q74=sQuery(id+"F2.wireOp",VERTEX,"347954fc-71f7-4e04-b67b-ed17862fd428.center");
            var Q75;
            Q75=sQuery(id+"F2.wireOp",VERTEX,"c2199767-ffbd-40b3-b06c-9cbd7b6d65c2.center");
            var Q76;
            Q76=sQuery(id+"F2.wireOp",VERTEX,"6e715679-a368-4c5c-95c6-8e90dc31b929.center");
            var Q77;
            Q77=sQuery(id+"F2.wireOp",VERTEX,"e16f9d6e-7c81-445f-826c-b792310ca58d.center");
            var Q78;
            Q78=sQuery(id+"F2.wireOp",VERTEX,"E182.center");
            var Q79;
            Q79=sQuery(id+"F2.wireOp",VERTEX,"E183.center");
            var Q80;
            Q80=sQuery(id+"F2.wireOp",VERTEX,"E184.center");
            var Q81;
            Q81=sQuery(id+"F2.wireOp",VERTEX,"E185.center");
            var Q82;
            Q82=sQuery(id+"F2.wireOp",VERTEX,"E186.center");
            var Q83;
            Q83=sQuery(id+"F2.wireOp",VERTEX,"E200.center");
            var Q84;
            Q84=sQuery(id+"F2.wireOp",VERTEX,"E201.center");
            var Q85;
            Q85=sQuery(id+"F2.wireOp",VERTEX,"E203.center");
            var Q86;
            Q86=sQuery(id+"F2.wireOp",VERTEX,"E202.center");
            var Q87;
            Q87=sQuery(id+"F2.wireOp",VERTEX,"E194.center");
            var Q88;
            Q88=sQuery(id+"F2.wireOp",VERTEX,"E195.center");
            var Q89;
            Q89=sQuery(id+"F2.wireOp",VERTEX,"E196.center");
            var Q90;
            Q90=sQuery(id+"F2.wireOp",VERTEX,"E193.center");
            var Q91;
            Q91=sQuery(id+"F2.wireOp",VERTEX,"E198.center");
            var Q92;
            Q92=sQuery(id+"F2.wireOp",VERTEX,"E199.center");
            var Q93;
            Q93=makeQuery(id+"F1.opExtrude","SWEPT_BODY",BODY,{"disambiguationData":[OSD([sQuery(id+"F0.wireOp",EDGE,"E0"),sQuery(id+"F0.wireOp",EDGE,"E1"),sQuery(id+"F0.wireOp",EDGE,"E2"),sQuery(id+"F0.wireOp",EDGE,"E3"),sQuery(id+"F0.wireOp",EDGE,"E4"),sQuery(id+"F0.wireOp",EDGE,"E5"),sQuery(id+"F0.wireOp",EDGE,"E6"),sQuery(id+"F0.wireOp",EDGE,"E7"),sQuery(id+"F0.wireOp",EDGE,"E8"),sQuery(id+"F0.wireOp",EDGE,"E9"),sQuery(id+"F0.wireOp",EDGE,"E10.MirrorCS"),sQuery(id+"F0.wireOp",EDGE,"E11.MirrorCS"),sQuery(id+"F0.wireOp",EDGE,"E12.MirrorCS"),sQuery(id+"F0.wireOp",EDGE,"E13.MirrorCS"),sQuery(id+"F0.wireOp",EDGE,"E14.MirrorCS"),sQuery(id+"F0.wireOp",EDGE,"E15.MirrorCS"),sQuery(id+"F0.wireOp",EDGE,"E16.MirrorCS"),sQuery(id+"F0.wireOp",EDGE,"E17.MirrorCS"),sQuery(id+"F0.wireOp",EDGE,"E18.MirrorCS"),sQuery(id+"F0.wireOp",EDGE,"E19.MirrorCS")])]});
            hole(context, id + "F6", {"style" : HoleStyle.SIMPLE, "endStyle" : HoleEndStyle.THROUGH, "holeDiameter" : 3 * mm, "locations" : qUnion([Q0, Q1, Q2, Q3, Q4, Q5, Q6, Q7, Q8, Q9, Q10, Q11, Q12, Q13, Q14, Q15, Q16, Q17, Q18, Q19, Q20, Q21, Q22, Q23, Q24, Q25, Q26, Q27, Q28, Q29, Q30, Q31, Q32, Q33, Q34, Q35, Q36, Q37, Q38, Q39, Q40, Q41, Q42, Q43, Q44, Q45, Q46, Q47, Q48, Q49, Q50, Q51, Q52, Q53, Q54, Q55, Q56, Q57, Q58, Q59, Q60, Q61, Q62, Q63, Q64, Q65, Q66, Q67, Q68, Q69, Q70, Q71, Q72, Q73, Q74, Q75, Q76, Q77, Q78, Q79, Q80, Q81, Q82, Q83, Q84, Q85, Q86, Q87, Q88, Q89, Q90, Q91, Q92]), "scope" : qUnion([Q93]), "isTappedThrough" : true});
        }
        {
            var Q0;
            Q0=sQuery(id+"F2.wireOp",VERTEX,"E141.center");
            var Q1;
            Q1=sQuery(id+"F2.wireOp",VERTEX,"E142.center");
            var Q2;
            Q2=sQuery(id+"F2.wireOp",VERTEX,"E143.center");
            var Q3;
            Q3=sQuery(id+"F2.wireOp",VERTEX,"E144.center");
            var Q4;
            Q4=sQuery(id+"F2.wireOp",VERTEX,"E140.center");
            var Q5;
            Q5=sQuery(id+"F2.wireOp",VERTEX,"E139.center");
            var Q6;
            Q6=sQuery(id+"F2.wireOp",VERTEX,"E145.center");
            var Q7;
            Q7=sQuery(id+"F2.wireOp",VERTEX,"E146.center");
            var Q8;
            Q8=sQuery(id+"F2.wireOp",VERTEX,"E148.center");
            var Q9;
            Q9=sQuery(id+"F2.wireOp",VERTEX,"E147.center");
            var Q10;
            Q10=sQuery(id+"F2.wireOp",VERTEX,"E149.center");
            var Q11;
            Q11=sQuery(id+"F2.wireOp",VERTEX,"E150.center");
            var Q12;
            Q12=sQuery(id+"F2.wireOp",VERTEX,"E168.center");
            var Q13;
            Q13=sQuery(id+"F2.wireOp",VERTEX,"E167.center");
            var Q14;
            Q14=sQuery(id+"F2.wireOp",VERTEX,"E166.center");
            var Q15;
            Q15=sQuery(id+"F2.wireOp",VERTEX,"E165.center");
            var Q16;
            Q16=sQuery(id+"F2.wireOp",VERTEX,"E158.center");
            var Q17;
            Q17=sQuery(id+"F2.wireOp",VERTEX,"E151.center");
            var Q18;
            Q18=sQuery(id+"F2.wireOp",VERTEX,"E152.center");
            var Q19;
            Q19=sQuery(id+"F2.wireOp",VERTEX,"E155.center");
            var Q20;
            Q20=sQuery(id+"F2.wireOp",VERTEX,"E153.center");
            var Q21;
            Q21=sQuery(id+"F2.wireOp",VERTEX,"E156.center");
            var Q22;
            Q22=sQuery(id+"F2.wireOp",VERTEX,"E154.center");
            var Q23;
            Q23=sQuery(id+"F2.wireOp",VERTEX,"E157.center");
            var Q24;
            Q24=sQuery(id+"F2.wireOp",VERTEX,"E159.center");
            var Q25;
            Q25=sQuery(id+"F2.wireOp",VERTEX,"E160.center");
            var Q26;
            Q26=sQuery(id+"F2.wireOp",VERTEX,"E156.center");
            var Q27;
            Q27=sQuery(id+"F2.wireOp",VERTEX,"E161.center");
            var Q28;
            Q28=sQuery(id+"F2.wireOp",VERTEX,"E163.center");
            var Q29;
            Q29=sQuery(id+"F2.wireOp",VERTEX,"E162.center");
            var Q30;
            Q30=sQuery(id+"F2.wireOp",VERTEX,"E164.center");
            var Q31;
            Q31=makeQuery(id+"F1.opExtrude","SWEPT_BODY",BODY,{"disambiguationData":[OSD([sQuery(id+"F0.wireOp",EDGE,"E0"),sQuery(id+"F0.wireOp",EDGE,"E1"),sQuery(id+"F0.wireOp",EDGE,"E2"),sQuery(id+"F0.wireOp",EDGE,"E3"),sQuery(id+"F0.wireOp",EDGE,"E4"),sQuery(id+"F0.wireOp",EDGE,"E5"),sQuery(id+"F0.wireOp",EDGE,"E6"),sQuery(id+"F0.wireOp",EDGE,"E7"),sQuery(id+"F0.wireOp",EDGE,"E8"),sQuery(id+"F0.wireOp",EDGE,"E9"),sQuery(id+"F0.wireOp",EDGE,"E10.MirrorCS"),sQuery(id+"F0.wireOp",EDGE,"E11.MirrorCS"),sQuery(id+"F0.wireOp",EDGE,"E12.MirrorCS"),sQuery(id+"F0.wireOp",EDGE,"E13.MirrorCS"),sQuery(id+"F0.wireOp",EDGE,"E14.MirrorCS"),sQuery(id+"F0.wireOp",EDGE,"E15.MirrorCS"),sQuery(id+"F0.wireOp",EDGE,"E16.MirrorCS"),sQuery(id+"F0.wireOp",EDGE,"E17.MirrorCS"),sQuery(id+"F0.wireOp",EDGE,"E18.MirrorCS"),sQuery(id+"F0.wireOp",EDGE,"E19.MirrorCS"),sQuery(id+"F0.wireOp",EDGE,"E20.top"),sQuery(id+"F0.wireOp",EDGE,"E20.left"),sQuery(id+"F0.wireOp",EDGE,"E20.right")])]});
            hole(context, id + "F7", {"style" : HoleStyle.C_SINK, "endStyle" : HoleEndStyle.THROUGH, "holeDiameter" : 3 * mm, "cSinkDiameter" : 5.7 * mm, "cSinkAngle" : 90 * degree, "locations" : qUnion([Q0, Q1, Q2, Q3, Q4, Q5, Q6, Q7, Q8, Q9, Q10, Q11, Q12, Q13, Q14, Q15, Q16, Q17, Q18, Q19, Q20, Q21, Q22, Q23, Q24, Q25, Q26, Q27, Q28, Q29, Q30]), "scope" : qUnion([Q31]), "isTappedThrough" : true});
        }
        {
            var Q0;
            Q0=makeQuery(id+"F2.imprint","IMPRINT",FACE,{"disambiguationData":[TD([[makeQuery(id+"F2.imprint","IMPRINT",EDGE,{"derivedFrom":sQuery(id+"F2.wireOp",EDGE,"E42.bottom")}),-1.0]])]});
            var Q1;
            Q1=makeQuery(id+"F2.imprint","IMPRINT",FACE,{"disambiguationData":[TD([[makeQuery(id+"F2.imprint","IMPRINT",EDGE,{"derivedFrom":sQuery(id+"F2.wireOp",EDGE,"E43.bottom")}),-1.0]])]});
            var Q2;
            Q2=makeQuery(id+"F2.imprint","IMPRINT",FACE,{"disambiguationData":[TD([[makeQuery(id+"F2.imprint","IMPRINT",EDGE,{"derivedFrom":sQuery(id+"F2.wireOp",EDGE,"E48.bottom")}),-1.0]])]});
            var Q3;
            Q3=makeQuery(id+"F2.imprint","IMPRINT",FACE,{"disambiguationData":[TD([[makeQuery(id+"F2.imprint","IMPRINT",EDGE,{"derivedFrom":sQuery(id+"F2.wireOp",EDGE,"E53.0")}),-1.0]])]});
            var Q4;
            Q4=makeQuery(id+"F2.imprint","IMPRINT",FACE,{"disambiguationData":[TD([[makeQuery(id+"F2.imprint","IMPRINT",EDGE,{"derivedFrom":sQuery(id+"F2.wireOp",EDGE,"E108.bottom")}),-1.0]])]});
            var Q5;
            Q5=makeQuery(id+"F2.imprint","IMPRINT",FACE,{"disambiguationData":[TD([[makeQuery(id+"F2.imprint","IMPRINT",EDGE,{"derivedFrom":sQuery(id+"F2.wireOp",EDGE,"E109.bottom")}),-1.0]])]});
            var Q6;
            Q6=makeQuery(id+"F2.imprint","IMPRINT",FACE,{"disambiguationData":[TD([[makeQuery(id+"F2.imprint","IMPRINT",EDGE,{"derivedFrom":sQuery(id+"F2.wireOp",EDGE,"E107.bottom")}),1.0]])]});
            var Q7;
            Q7=makeQuery(id+"F2.imprint","IMPRINT",FACE,{"disambiguationData":[TD([[makeQuery(id+"F2.imprint","IMPRINT",EDGE,{"derivedFrom":sQuery(id+"F2.wireOp",EDGE,"E106.bottom")}),1.0]])]});
            var Q8;
            Q8=makeQuery(id+"F2.imprint","IMPRINT",FACE,{"disambiguationData":[TD([[makeQuery(id+"F2.imprint","IMPRINT",EDGE,{"derivedFrom":sQuery(id+"F2.wireOp",EDGE,"E105.bottom")}),1.0]])]});
            var Q9;
            Q9=makeQuery(id+"F2.imprint","IMPRINT",FACE,{"disambiguationData":[TD([[makeQuery(id+"F2.imprint","IMPRINT",EDGE,{"derivedFrom":sQuery(id+"F2.wireOp",EDGE,"E104.bottom")}),1.0]])]});
            var Q10;
            Q10=makeQuery(id+"F2.imprint","IMPRINT",FACE,{"disambiguationData":[TD([[makeQuery(id+"F2.imprint","IMPRINT",EDGE,{"derivedFrom":sQuery(id+"F2.wireOp",EDGE,"E102.bottom")}),-1.0]])]});
            var Q11;
            Q11=makeQuery(id+"F2.imprint","IMPRINT",FACE,{"disambiguationData":[TD([[makeQuery(id+"F2.imprint","IMPRINT",EDGE,{"derivedFrom":sQuery(id+"F2.wireOp",EDGE,"E100.bottom")}),-1.0]])]});
            var Q12;
            Q12=makeQuery(id+"F2.imprint","IMPRINT",FACE,{"disambiguationData":[TD([[makeQuery(id+"F2.imprint","IMPRINT",EDGE,{"derivedFrom":sQuery(id+"F2.wireOp",EDGE,"E103.bottom")}),1.0]])]});
            var Q13;
            Q13=makeQuery(id+"F2.imprint","IMPRINT",FACE,{"disambiguationData":[TD([[makeQuery(id+"F2.imprint","IMPRINT",EDGE,{"derivedFrom":sQuery(id+"F2.wireOp",EDGE,"E101.bottom")}),-1.0]])]});
            var Q14;
            Q14=makeQuery(id+"F2.imprint","IMPRINT",FACE,{"disambiguationData":[TD([[makeQuery(id+"F2.imprint","IMPRINT",EDGE,{"derivedFrom":sQuery(id+"F2.wireOp",EDGE,"E98.0")}),-1.0]])]});
            var Q15;
            Q15=makeQuery(id+"F2.imprint","IMPRINT",FACE,{"disambiguationData":[TD([[makeQuery(id+"F2.imprint","IMPRINT",EDGE,{"derivedFrom":sQuery(id+"F2.wireOp",EDGE,"E110.bottom")}),1.0]])]});
            var Q16;
            Q16=makeQuery(id+"F2.imprint","IMPRINT",FACE,{"disambiguationData":[TD([[makeQuery(id+"F2.imprint","IMPRINT",EDGE,{"derivedFrom":sQuery(id+"F2.wireOp",EDGE,"E55.bottom")}),-1.0]])]});
            var Q17;
            Q17=makeQuery(id+"F2.imprint","IMPRINT",FACE,{"disambiguationData":[TD([[makeQuery(id+"F2.imprint","IMPRINT",EDGE,{"derivedFrom":sQuery(id+"F2.wireOp",EDGE,"E56.bottom")}),-1.0]])]});
            var Q18;
            Q18=makeQuery(id+"F2.imprint","IMPRINT",FACE,{"disambiguationData":[TD([[makeQuery(id+"F2.imprint","IMPRINT",EDGE,{"derivedFrom":sQuery(id+"F2.wireOp",EDGE,"E57.bottom")}),-1.0]])]});
            var Q19;
            Q19=makeQuery(id+"F2.imprint","IMPRINT",FACE,{"disambiguationData":[TD([[makeQuery(id+"F2.imprint","IMPRINT",EDGE,{"derivedFrom":sQuery(id+"F2.wireOp",EDGE,"E118.bottom")}),1.0]])]});
            var Q20;
            Q20=makeQuery(id+"F2.imprint","IMPRINT",FACE,{"disambiguationData":[TD([[makeQuery(id+"F2.imprint","IMPRINT",EDGE,{"derivedFrom":sQuery(id+"F2.wireOp",EDGE,"E117.bottom")}),1.0]])]});
            var Q21;
            Q21=makeQuery(id+"F2.imprint","IMPRINT",FACE,{"disambiguationData":[TD([[makeQuery(id+"F2.imprint","IMPRINT",EDGE,{"derivedFrom":sQuery(id+"F2.wireOp",EDGE,"E116.bottom")}),1.0]])]});
            var Q22;
            Q22=makeQuery(id+"F2.imprint","IMPRINT",FACE,{"disambiguationData":[TD([[makeQuery(id+"F2.imprint","IMPRINT",EDGE,{"derivedFrom":sQuery(id+"F2.wireOp",EDGE,"E115.bottom")}),1.0]])]});
            var Q23;
            Q23=makeQuery(id+"F2.imprint","IMPRINT",FACE,{"disambiguationData":[TD([[makeQuery(id+"F2.imprint","IMPRINT",EDGE,{"derivedFrom":sQuery(id+"F2.wireOp",EDGE,"a7078a2f-d097-49b7-9cdb-dcde8b9ae8b5.0")}),-1.0]])]});
            var Q24;
            Q24=makeQuery(id+"F2.imprint","IMPRINT",FACE,{"disambiguationData":[TD([[makeQuery(id+"F2.imprint","IMPRINT",EDGE,{"derivedFrom":sQuery(id+"F2.wireOp",EDGE,"E122.bottom")}),1.0]])]});
            var Q25;
            Q25=makeQuery(id+"F2.imprint","IMPRINT",FACE,{"disambiguationData":[TD([[makeQuery(id+"F2.imprint","IMPRINT",EDGE,{"derivedFrom":sQuery(id+"F2.wireOp",EDGE,"E123.bottom")}),-1.0]])]});
            var Q26;
            Q26=makeQuery(id+"F2.imprint","IMPRINT",FACE,{"disambiguationData":[TD([[makeQuery(id+"F2.imprint","IMPRINT",EDGE,{"derivedFrom":sQuery(id+"F2.wireOp",EDGE,"E121.bottom")}),-1.0]])]});
            var Q27;
            Q27=makeQuery(id+"F2.imprint","IMPRINT",FACE,{"disambiguationData":[TD([[makeQuery(id+"F2.imprint","IMPRINT",EDGE,{"derivedFrom":sQuery(id+"F2.wireOp",EDGE,"E119.bottom")}),-1.0]])]});
            var Q28;
            Q28=makeQuery(id+"F2.imprint","IMPRINT",FACE,{"disambiguationData":[TD([[makeQuery(id+"F2.imprint","IMPRINT",EDGE,{"derivedFrom":sQuery(id+"F2.wireOp",EDGE,"E120.bottom")}),-1.0]])]});
            var Q29;
            Q29=makeQuery(id+"F2.imprint","IMPRINT",FACE,{"disambiguationData":[TD([[makeQuery(id+"F2.imprint","IMPRINT",EDGE,{"derivedFrom":sQuery(id+"F2.wireOp",EDGE,"E138.bottom")}),-1.0]])]});
            var Q30;
            Q30=makeQuery(id+"F2.imprint","IMPRINT",FACE,{"disambiguationData":[TD([[makeQuery(id+"F2.imprint","IMPRINT",EDGE,{"derivedFrom":sQuery(id+"F2.wireOp",EDGE,"E169")}),-1.0]])]});
            var Q31;
            Q31=makeQuery(id+"F2.imprint","IMPRINT",FACE,{"disambiguationData":[TD([[makeQuery(id+"F2.imprint","IMPRINT",EDGE,{"derivedFrom":sQuery(id+"F2.wireOp",EDGE,"E187")}),-1.0]])]});
            var Q32;
            Q32=makeQuery(id+"F2.imprint","IMPRINT",FACE,{"disambiguationData":[TD([[makeQuery(id+"F2.imprint","IMPRINT",EDGE,{"derivedFrom":sQuery(id+"F2.wireOp",EDGE,"E197.bottom")}),-1.0]])]});
            var Q33;
            Q33=makeQuery(id+"F2.imprint","IMPRINT",FACE,{"disambiguationData":[TD([[makeQuery(id+"F2.imprint","IMPRINT",EDGE,{"derivedFrom":sQuery(id+"F2.wireOp",EDGE,"E192")}),1.0]])]});
            extrude(context, id + "F8", {"entities" : qUnion([Q0, Q1, Q2, Q3, Q4, Q5, Q6, Q7, Q8, Q9, Q10, Q11, Q12, Q13, Q14, Q15, Q16, Q17, Q18, Q19, Q20, Q21, Q22, Q23, Q24, Q25, Q26, Q27, Q28, Q29, Q30, Q31, Q32, Q33]), "operationType" : NewBodyOperationType.REMOVE, "oppositeDirection" : true, "depth" : 3 * mm});
        }
        {
            var Q0;
            Q0=qCreatedBy(makeId("Front.planeOp"),FACE);
            var sketch = newSketch(context, id + "F9", { "sketchPlane" : qUnion([Q0])});
            skLineSegment(sketch, "E212.bottom", {"start": v(150, 480) * mm, "end": v(-150, 480) * mm});
            skLineSegment(sketch, "E212.top", {"start": v(150, 450) * mm, "end": v(-150, 450) * mm});
            skLineSegment(sketch, "E212.left", {"start": v(150, 480) * mm, "end": v(150, 450) * mm});
            skLineSegment(sketch, "E212.right", {"start": v(-150, 480) * mm, "end": v(-150, 450) * mm});
            skPoint(sketch, "E212.middle", {"position": v(0, 465) * mm});
            skLineSegment(sketch, "E213.bottom", {"start": v(150, 0) * mm, "end": v(-150, 0) * mm});
            skLineSegment(sketch, "E213.top", {"start": v(150, 30) * mm, "end": v(-150, 30) * mm});
            skLineSegment(sketch, "E213.left", {"start": v(150, 0) * mm, "end": v(150, 30) * mm});
            skLineSegment(sketch, "E213.right", {"start": v(-150, 0) * mm, "end": v(-150, 30) * mm});
            skPoint(sketch, "E213.middle", {"position": v(0, 15) * mm});
            skSolve(sketch);
        }
        {
            var Q0;
            Q0=qSketchRegion(id+"F9",true);
            extrude(context, id + "F10", {"entities" : qUnion([Q0]), "oppositeDirection" : true, "depth" : 3 * mm});
        }
        {
            var Q0;
            Q0=sQuery(id+"F5.wireOp",VERTEX,"E205.center");
            var Q1;
            Q1=sQuery(id+"F5.wireOp",VERTEX,"E204.center");
            var Q2;
            Q2=sQuery(id+"F5.wireOp",VERTEX,"E211.MirrorC.center");
            var Q3;
            Q3=sQuery(id+"F5.wireOp",VERTEX,"E210.MirrorC.center");
            var Q4;
            Q4=sQuery(id+"F5.wireOp",VERTEX,"E207.center");
            var Q5;
            Q5=sQuery(id+"F5.wireOp",VERTEX,"E206.center");
            var Q6;
            Q6=sQuery(id+"F5.wireOp",VERTEX,"E209.MirrorC.center");
            var Q7;
            Q7=sQuery(id+"F5.wireOp",VERTEX,"E208.MirrorC.center");
            var Q8;
            Q8=makeQuery(id+"F1.opExtrude","SWEPT_BODY",BODY,{"disambiguationData":[OSD([sQuery(id+"F0.wireOp",EDGE,"E0"),sQuery(id+"F0.wireOp",EDGE,"E1"),sQuery(id+"F0.wireOp",EDGE,"E2"),sQuery(id+"F0.wireOp",EDGE,"E3"),sQuery(id+"F0.wireOp",EDGE,"E4"),sQuery(id+"F0.wireOp",EDGE,"E5"),sQuery(id+"F0.wireOp",EDGE,"E6"),sQuery(id+"F0.wireOp",EDGE,"E7"),sQuery(id+"F0.wireOp",EDGE,"E8"),sQuery(id+"F0.wireOp",EDGE,"E9"),sQuery(id+"F0.wireOp",EDGE,"E10.MirrorCS"),sQuery(id+"F0.wireOp",EDGE,"E11.MirrorCS"),sQuery(id+"F0.wireOp",EDGE,"E12.MirrorCS"),sQuery(id+"F0.wireOp",EDGE,"E13.MirrorCS"),sQuery(id+"F0.wireOp",EDGE,"E14.MirrorCS"),sQuery(id+"F0.wireOp",EDGE,"E15.MirrorCS"),sQuery(id+"F0.wireOp",EDGE,"E16.MirrorCS"),sQuery(id+"F0.wireOp",EDGE,"E17.MirrorCS"),sQuery(id+"F0.wireOp",EDGE,"E18.MirrorCS"),sQuery(id+"F0.wireOp",EDGE,"E19.MirrorCS")])]});
            var Q9;
            Q9=makeQuery(id+"F10.opExtrude","SWEPT_BODY",BODY,{"disambiguationData":[OSD([sQuery(id+"F9.wireOp",EDGE,"E212.bottom"),sQuery(id+"F9.wireOp",EDGE,"E212.top"),sQuery(id+"F9.wireOp",EDGE,"E212.left"),sQuery(id+"F9.wireOp",EDGE,"E212.right")])]});
            var Q10;
            Q10=makeQuery(id+"F10.opExtrude","SWEPT_BODY",BODY,{"disambiguationData":[OSD([sQuery(id+"F9.wireOp",EDGE,"E213.bottom"),sQuery(id+"F9.wireOp",EDGE,"E213.top"),sQuery(id+"F9.wireOp",EDGE,"E213.left"),sQuery(id+"F9.wireOp",EDGE,"E213.right")])]});
            hole(context, id + "F11", {"style" : HoleStyle.SIMPLE, "endStyle" : HoleEndStyle.THROUGH, "holeDiameter" : 5 * mm, "locations" : qUnion([Q0, Q1, Q2, Q3, Q4, Q5, Q6, Q7]), "scope" : qUnion([Q8, Q9, Q10]), "isTappedThrough" : true});
        }
        {
            var Q0;
            Q0=makeQuery(id+"F10.opExtrude","CAP_FACE",FACE,{"disambiguationData":[OSD([sQuery(id+"F9.wireOp",EDGE,"E213.bottom"),sQuery(id+"F9.wireOp",EDGE,"E213.top"),sQuery(id+"F9.wireOp",EDGE,"E213.left"),sQuery(id+"F9.wireOp",EDGE,"E213.right")])],"isStart":false});
            var sketch = newSketch(context, id + "F12", { "sketchPlane" : qUnion([Q0])});
            skLineSegment(sketch, "E214.bottom", {"start": v(-150, 480) * mm, "end": v(-145, 480) * mm});
            skLineSegment(sketch, "E214.top", {"start": v(-150, 450) * mm, "end": v(-145, 450) * mm});
            skLineSegment(sketch, "E214.left", {"start": v(-150, 480) * mm, "end": v(-150, 450) * mm});
            skLineSegment(sketch, "E214.right", {"start": v(-145, 480) * mm, "end": v(-145, 450) * mm});
            skLineSegment(sketch, "E215.bottom", {"start": v(150, 480) * mm, "end": v(145, 480) * mm});
            skLineSegment(sketch, "E215.top", {"start": v(150, 450) * mm, "end": v(145, 450) * mm});
            skLineSegment(sketch, "E215.left", {"start": v(150, 480) * mm, "end": v(150, 450) * mm});
            skLineSegment(sketch, "E215.right", {"start": v(145, 480) * mm, "end": v(145, 450) * mm});
            skLineSegment(sketch, "E216.bottom", {"start": v(-150, 30) * mm, "end": v(-145, 30) * mm});
            skLineSegment(sketch, "E216.top", {"start": v(-150, 0) * mm, "end": v(-145, 0) * mm});
            skLineSegment(sketch, "E216.left", {"start": v(-150, 30) * mm, "end": v(-150, 0) * mm});
            skLineSegment(sketch, "E216.right", {"start": v(-145, 30) * mm, "end": v(-145, 0) * mm});
            skLineSegment(sketch, "E217.bottom", {"start": v(150, 30) * mm, "end": v(145, 30) * mm});
            skLineSegment(sketch, "E217.top", {"start": v(150, 0) * mm, "end": v(145, 0) * mm});
            skLineSegment(sketch, "E217.left", {"start": v(150, 30) * mm, "end": v(150, 0) * mm});
            skLineSegment(sketch, "E217.right", {"start": v(145, 30) * mm, "end": v(145, 0) * mm});
            skSolve(sketch);
        }
        {
            var Q0;
            Q0=qSketchRegion(id+"F12",true);
            extrude(context, id + "F13", {"entities" : qUnion([Q0]), "operationType" : NewBodyOperationType.ADD, "depth" : 100 * mm});
        }
        {
            var Q0;
            Q0=makeQuery(id+"F13.boolean.opBoolean","MERGE",FACE,{"derivedFrom":[makeQuery(id+"F10.opExtrude","SWEPT_FACE",FACE,{"disambiguationData":[OSD([sQuery(id+"F9.wireOp",EDGE,"E212.left")])]}),makeQuery(id+"F13.opExtrude","SWEPT_FACE",FACE,{"disambiguationData":[OSD([sQuery(id+"F12.wireOp",EDGE,"E214.left")])]})]});
            var sketch = newSketch(context, id + "F14", { "sketchPlane" : qUnion([Q0])});
            skLineSegment(sketch, "E218", {"start": v(103, 480) * mm, "end": v(135.54, 480) * mm});
            skLineSegment(sketch, "E219", {"start": v(135.54, 480) * mm, "end": v(135.54, -334.5) * mm});
            skLineSegment(sketch, "E220", {"start": v(135.54, -334.5) * mm, "end": v(-92.54, -334.5) * mm});
            skLineSegment(sketch, "E221", {"start": v(-92.54, -334.5) * mm, "end": v(103, 480) * mm});
            skSolve(sketch);
        }
        {
            var Q0;
            Q0=qSketchRegion(id+"F14",true);
            extrude(context, id + "F15", {"entities" : qUnion([Q0]), "oppositeDirection" : true, "depth" : 300 * mm});
        }
        {
            var Q0;
            Q0=qCreatedBy(makeId("Right.planeOp"),FACE);
            var Q1;
            Q1=makeQuery(id+"F13.opExtrude","CAP_VERTEX",VERTEX,{"disambiguationData":[OSD([sQuery(id+"F12.wireOp",EDGE,"E214.bottom"),sQuery(id+"F12.wireOp",EDGE,"E214.right")])],"isStart":false});
            cPlane(context, id + "F16", {"entities" : qUnion([Q0, Q1]), "cplaneType" : CPlaneType.PLANE_POINT, "offset" : 25 * mm, "width" : 150 * mm, "height" : 150 * mm});
        }
        {
            var Q0;
            Q0=qCreatedBy(id+"F16.planeOp",FACE);
            var sketch = newSketch(context, id + "F17", { "sketchPlane" : qUnion([Q0])});
            skLineSegment(sketch, "E222", {"start": v(135.54, 475) * mm, "end": v(135.54, -334.5) * mm});
            skLineSegment(sketch, "E223", {"start": v(135.54, -334.5) * mm, "end": v(-87.4, -334.5) * mm});
            skLineSegment(sketch, "E224", {"start": v(-87.4, -334.5) * mm, "end": v(106.94, 475) * mm});
            skLineSegment(sketch, "E225", {"start": v(106.94, 475) * mm, "end": v(135.54, 475) * mm});
            skSolve(sketch);
        }
        {
            var Q0;
            Q0=qSketchRegion(id+"F17",true);
            extrude(context, id + "F18", {"entities" : qUnion([Q0]), "operationType" : NewBodyOperationType.REMOVE, "oppositeDirection" : true, "depth" : 290 * mm});
        }
        {
            var Q0;
            Q0=qCreatedBy(makeId("Top.planeOp"),FACE);
            var Q1;
            Q1=sQuery(id+"F14.wireOp",VERTEX,"E221.start");
            cPlane(context, id + "F19", {"entities" : qUnion([Q0, Q1]), "cplaneType" : CPlaneType.PLANE_POINT, "offset" : 25 * mm, "width" : 150 * mm, "height" : 150 * mm});
        }
        {
            var Q0;
            Q0=qCreatedBy(makeId("Front.planeOp"),FACE);
            var sketch = newSketch(context, id + "F20", { "sketchPlane" : qUnion([Q0])});
            skLineSegment(sketch, "E226.bottom", {"start": v(378.73, -232.42) * mm, "end": v(381.73, -232.42) * mm});
            skLineSegment(sketch, "E226.top", {"start": v(378.73, -265.42) * mm, "end": v(411.73, -265.42) * mm});
            skLineSegment(sketch, "E226.left", {"start": v(378.73, -232.42) * mm, "end": v(378.73, -265.42) * mm});
            skLineSegment(sketch, "E226.right", {"start": v(411.73, -262.42) * mm, "end": v(411.73, -265.42) * mm});
            skLineSegment(sketch, "E227.top", {"start": v(381.73, -262.42) * mm, "end": v(411.73, -262.42) * mm});
            skLineSegment(sketch, "E227.left", {"start": v(381.73, -232.42) * mm, "end": v(381.73, -262.42) * mm});
            skSolve(sketch);
        }
        {
            var Q0;
            Q0=qSketchRegion(id+"F20",true);
            extrude(context, id + "F21", {"entities" : qUnion([Q0]), "depth" : 50 * mm});
        }
        {
            var Q0;
            Q0=makeQuery(id+"F21.opExtrude","SWEPT_FACE",FACE,{"disambiguationData":[OSD([sQuery(id+"F20.wireOp",EDGE,"E227.top")])]});
            var sketch = newSketch(context, id + "F22", { "sketchPlane" : qUnion([Q0])});
            skCircle(sketch, "E228", {"center": v(396.73, -35) * mm, "radius": 2.5 * mm});
            skCircle(sketch, "E229", {"center": v(396.73, -15) * mm, "radius": 2.47 * mm});
            skSolve(sketch);
        }
        {
            var Q0;
            Q0=makeQuery(id+"F21.opExtrude","SWEPT_FACE",FACE,{"disambiguationData":[OSD([sQuery(id+"F20.wireOp",EDGE,"E227.left")])]});
            var sketch = newSketch(context, id + "F23", { "sketchPlane" : qUnion([Q0])});
            skCircle(sketch, "E230", {"center": v(-35, -247.42) * mm, "radius": 2.5 * mm});
            skCircle(sketch, "E231", {"center": v(-15, -247.42) * mm, "radius": 2.5 * mm});
            skSolve(sketch);
        }
        {
            var Q0;
            Q0=sQuery(id+"F23.wireOp",VERTEX,"E230.center");
            var Q1;
            Q1=sQuery(id+"F23.wireOp",VERTEX,"E231.center");
            var Q2;
            Q2=sQuery(id+"F22.wireOp",VERTEX,"E229.center");
            var Q3;
            Q3=sQuery(id+"F22.wireOp",VERTEX,"E228.center");
            var Q4;
            Q4=makeQuery(id+"F21.opExtrude","SWEPT_BODY",BODY,{"disambiguationData":[OSD([sQuery(id+"F20.wireOp",EDGE,"E226.bottom"),sQuery(id+"F20.wireOp",EDGE,"E226.top"),sQuery(id+"F20.wireOp",EDGE,"E226.left"),sQuery(id+"F20.wireOp",EDGE,"E226.right"),sQuery(id+"F20.wireOp",EDGE,"E227.top"),sQuery(id+"F20.wireOp",EDGE,"E227.left")])]});
            hole(context, id + "F24", {"style" : HoleStyle.SIMPLE, "endStyle" : HoleEndStyle.THROUGH, "holeDiameter" : 5 * mm, "locations" : qUnion([Q0, Q1, Q2, Q3]), "scope" : qUnion([Q4]), "isTappedThrough" : true});
        }
        {
            var Q0;
            Q0=makeQuery(id+"F21.opExtrude","CAP_EDGE",EDGE,{"disambiguationData":[OSD([sQuery(id+"F20.wireOp",EDGE,"E226.right")])],"isStart":false});
            var Q1;
            Q1=makeQuery(id+"F21.opExtrude","CAP_EDGE",EDGE,{"disambiguationData":[OSD([sQuery(id+"F20.wireOp",EDGE,"E226.right")])],"isStart":true});
            var Q2;
            Q2=makeQuery(id+"F21.opExtrude","CAP_EDGE",EDGE,{"disambiguationData":[OSD([sQuery(id+"F20.wireOp",EDGE,"E226.bottom")])],"isStart":false});
            var Q3;
            Q3=makeQuery(id+"F21.opExtrude","CAP_EDGE",EDGE,{"disambiguationData":[OSD([sQuery(id+"F20.wireOp",EDGE,"E226.bottom")])],"isStart":true});
            var Q4;
            Q4=makeQuery(id+"F21.opExtrude","SWEPT_EDGE",EDGE,{"disambiguationData":[OSD([sQuery(id+"F20.wireOp",EDGE,"E226.top"),sQuery(id+"F20.wireOp",EDGE,"E226.left")])]});
            var Q5;
            Q5=makeQuery(id+"F21.opExtrude","SWEPT_EDGE",EDGE,{"disambiguationData":[OSD([sQuery(id+"F20.wireOp",EDGE,"E227.top"),sQuery(id+"F20.wireOp",EDGE,"E227.left")])]});
            fillet(context, id + "F25", {"entities" : qUnion([Q0, Q1, Q2, Q3, Q4, Q5]), "radius" : 5 * mm, "tangentPropagation" : true, "allowEdgeOverflow" : false});
        }
        {
            var Q0;
            {var subQ5=sQuery(id+"F14.wireOp",EDGE,"E218");Q0=makeQuery(id+"F14.imprint","IMPRINT",FACE,{"disambiguationData":[TD([[makeQuery(id+"F14.imprint","IMPRINT",EDGE,{"derivedFrom":subQ5}),-1.0]])]});}
            var sketch = newSketch(context, id + "F26", { "sketchPlane" : qUnion([Q0])});
            skCircle(sketch, "E232", {"center": v(105.54, -316.5) * mm, "radius": 2.5 * mm});
            skCircle(sketch, "E233", {"center": v(85.54, -316.5) * mm, "radius": 2.5 * mm});
            skCircle(sketch, "E234", {"center": v(-42.54, -316.5) * mm, "radius": 2.5 * mm});
            skCircle(sketch, "E235", {"center": v(-62.54, -316.5) * mm, "radius": 2.5 * mm});
            skSolve(sketch);
        }
        {
            var Q0;
            Q0=sQuery(id+"F26.wireOp",VERTEX,"E233.center");
            var Q1;
            Q1=sQuery(id+"F26.wireOp",VERTEX,"E232.center");
            var Q2;
            Q2=sQuery(id+"F26.wireOp",VERTEX,"E234.center");
            var Q3;
            Q3=sQuery(id+"F26.wireOp",VERTEX,"E235.center");
            var Q4;
            Q4=makeQuery(id+"F15.opExtrude","SWEPT_BODY",BODY,{"disambiguationData":[OSD([sQuery(id+"F14.wireOp",EDGE,"E218"),sQuery(id+"F14.wireOp",EDGE,"E219"),sQuery(id+"F14.wireOp",EDGE,"E220"),sQuery(id+"F14.wireOp",EDGE,"E221")])]});
            hole(context, id + "F27", {"style" : HoleStyle.SIMPLE, "endStyle" : HoleEndStyle.THROUGH, "holeDiameter" : 5 * mm, "locations" : qUnion([Q0, Q1, Q2, Q3]), "scope" : qUnion([Q4]), "isTappedThrough" : true});
        }
        {
            var Q0;
            Q0=qCreatedBy(makeId("Front.planeOp"),FACE);
            cPlane(context, id + "F28", {"entities" : qUnion([Q0]), "cplaneType" : CPlaneType.OFFSET, "offset" : 10 * mm, "oppositeDirection" : true, "width" : 150 * mm, "height" : 150 * mm});
        }
        {
            var Q0;
            Q0=qCreatedBy(id+"F28.planeOp",FACE);
            var sketch = newSketch(context, id + "F29", { "sketchPlane" : qUnion([Q0])});
            skLineSegment(sketch, "E236.bottom", {"start": v(1373.24, -207.85) * mm, "end": v(775.36, -207.85) * mm});
            skLineSegment(sketch, "E236.top", {"start": v(1373.24, 128.46) * mm, "end": v(775.36, 128.46) * mm});
            skLineSegment(sketch, "E236.left", {"start": v(1373.24, -207.85) * mm, "end": v(1373.24, 128.46) * mm});
            skLineSegment(sketch, "E236.right", {"start": v(775.36, -207.85) * mm, "end": v(775.36, 128.46) * mm});
            skLineSegment(sketch, "E237.bottom", {"start": v(1381, -224.28) * mm, "end": v(767.6, -224.28) * mm});
            skLineSegment(sketch, "E237.top", {"start": v(1381, 136.22) * mm, "end": v(767.6, 136.22) * mm});
            skLineSegment(sketch, "E237.left", {"start": v(1381, -224.28) * mm, "end": v(1381, 136.22) * mm});
            skLineSegment(sketch, "E237.right", {"start": v(767.6, -224.28) * mm, "end": v(767.6, 136.22) * mm});
            skLineSegment(sketch, "E238.bottom", {"start": v(546.2, 111.86) * mm, "end": v(-6.77, 111.86) * mm});
            skLineSegment(sketch, "E238.top", {"start": v(546.2, 420.5) * mm, "end": v(-6.77, 420.5) * mm});
            skLineSegment(sketch, "E238.left", {"start": v(546.2, 111.86) * mm, "end": v(546.2, 420.5) * mm});
            skLineSegment(sketch, "E238.right", {"start": v(-6.77, 111.86) * mm, "end": v(-6.77, 420.5) * mm});
            skPoint(sketch, "E238.middle", {"position": v(269.71, 266.18) * mm});
            skLineSegment(sketch, "E239.bottom", {"start": v(558.21, 85.5) * mm, "end": v(-18.79, 85.5) * mm});
            skLineSegment(sketch, "E239.top", {"start": v(558.21, 431.5) * mm, "end": v(-18.79, 431.5) * mm});
            skLineSegment(sketch, "E239.left", {"start": v(558.21, 85.5) * mm, "end": v(558.21, 431.5) * mm});
            skLineSegment(sketch, "E239.right", {"start": v(-18.79, 85.5) * mm, "end": v(-18.79, 431.5) * mm});
            skPoint(sketch, "E239.middle", {"position": v(269.71, 258.5) * mm});
            skLineSegment(sketch, "E240.bottom", {"start": v(-217.97, 98.58) * mm, "end": v(-555.89, 98.58) * mm});
            skLineSegment(sketch, "E240.top", {"start": v(-217.97, 368.92) * mm, "end": v(-555.89, 368.92) * mm});
            skLineSegment(sketch, "E240.left", {"start": v(-217.97, 98.58) * mm, "end": v(-217.97, 368.92) * mm});
            skLineSegment(sketch, "E240.right", {"start": v(-555.89, 98.58) * mm, "end": v(-555.89, 368.92) * mm});
            skPoint(sketch, "E240.middle", {"position": v(-386.93, 233.75) * mm});
            skLineSegment(sketch, "E241.bottom", {"start": v(-207.68, 85.5) * mm, "end": v(-566.18, 85.5) * mm});
            skLineSegment(sketch, "E241.top", {"start": v(-207.68, 382) * mm, "end": v(-566.18, 382) * mm});
            skLineSegment(sketch, "E241.left", {"start": v(-207.68, 85.5) * mm, "end": v(-207.68, 382) * mm});
            skLineSegment(sketch, "E241.right", {"start": v(-566.18, 85.5) * mm, "end": v(-566.18, 382) * mm});
            skSolve(sketch);
        }
        {
            var Q0;
            Q0=qCreatedBy(id+"F19.planeOp",FACE);
            var sketch = newSketch(context, id + "F30", { "sketchPlane" : qUnion([Q0])});
            skLineSegment(sketch, "E242.bottom", {"start": v(-812.5, -47.77) * mm, "end": v(812.5, -47.77) * mm});
            skLineSegment(sketch, "E242.top", {"start": v(-812.5, -597.77) * mm, "end": v(812.5, -597.77) * mm});
            skLineSegment(sketch, "E242.left", {"start": v(-812.5, -47.77) * mm, "end": v(-812.5, -597.77) * mm});
            skLineSegment(sketch, "E242.right", {"start": v(812.5, -47.77) * mm, "end": v(812.5, -597.77) * mm});
            skLineSegment(sketch, "E243", {"start": v(-812.5, -47.77) * mm, "end": v(-750, 282.23) * mm});
            skLineSegment(sketch, "E244", {"start": v(-750, 282.23) * mm, "end": v(750, 277.92) * mm});
            skLineSegment(sketch, "E245", {"start": v(750, 277.92) * mm, "end": v(812.5, -47.77) * mm});
            skLineSegment(sketch, "E246", {"start": v(-750, 282.23) * mm, "end": v(-650, 612.23) * mm});
            skLineSegment(sketch, "E247", {"start": v(-650, 612.23) * mm, "end": v(650, 614.48) * mm});
            skLineSegment(sketch, "E248", {"start": v(650, 614.48) * mm, "end": v(750, 277.92) * mm});
            skLineSegment(sketch, "E249", {"start": v(-650, 612.23) * mm, "end": v(-400, 932.23) * mm});
            skLineSegment(sketch, "E250", {"start": v(-400, 932.23) * mm, "end": v(400, 932.23) * mm});
            skLineSegment(sketch, "E251", {"start": v(400, 932.23) * mm, "end": v(650, 614.48) * mm});
            skLineSegment(sketch, "E252", {"start": v(0, 448.77) * mm, "end": v(0, -1817.13) * mm, "construction": true});
            skLineSegment(sketch, "E253", {"start": v(-400, 932.23) * mm, "end": v(-200, 1052.23) * mm});
            skLineSegment(sketch, "E254", {"start": v(-200, 1052.23) * mm, "end": v(200, 1052.19) * mm});
            skLineSegment(sketch, "E255", {"start": v(200, 1052.19) * mm, "end": v(400, 932.23) * mm});
            skCircle(sketch, "E256", {"center": v(168, 85.54) * mm, "radius": 2.5 * mm});
            skCircle(sketch, "E257", {"center": v(168, 105.54) * mm, "radius": 2.5 * mm});
            skCircle(sketch, "E258", {"center": v(168, -42.54) * mm, "radius": 2.5 * mm});
            skCircle(sketch, "E259", {"center": v(168, -62.54) * mm, "radius": 2.5 * mm});
            skCircle(sketch, "E260.MirrorC", {"center": v(-168, -62.54) * mm, "radius": 2.5 * mm});
            skCircle(sketch, "E261.MirrorC", {"center": v(-168, -42.54) * mm, "radius": 2.5 * mm});
            skCircle(sketch, "E262.MirrorC", {"center": v(-168, 85.54) * mm, "radius": 2.5 * mm});
            skCircle(sketch, "E263.MirrorC", {"center": v(-168, 105.54) * mm, "radius": 2.5 * mm});
            skSolve(sketch);
        }
        {
            var Q0;
            Q0=qSketchRegion(id+"F30",true);
            extrude(context, id + "F31", {"entities" : qUnion([Q0]), "oppositeDirection" : true, "depth" : 5 * mm});
        }
        {
            var Q0;
            Q0=qCreatedBy(makeId("Right.planeOp"),FACE);
            cPlane(context, id + "F32", {"entities" : qUnion([Q0]), "cplaneType" : CPlaneType.OFFSET, "offset" : 192.5 * mm, "oppositeDirection" : true, "width" : 150 * mm, "height" : 150 * mm});
        }
        {
            var Q0;
            Q0=qCreatedBy(id+"F32.planeOp",FACE);
            var sketch = newSketch(context, id + "F33", { "sketchPlane" : qUnion([Q0])});
            skLineSegment(sketch, "E264", {"start": v(-103.13, 25.5) * mm, "end": v(-103.13, -334.5) * mm});
            skLineSegment(sketch, "E265", {"start": v(-103.13, -334.5) * mm, "end": v(-758.97, -334.5) * mm});
            skLineSegment(sketch, "E266", {"start": v(-758.97, -334.5) * mm, "end": v(-758.97, -84.5) * mm});
            skLineSegment(sketch, "E267", {"start": v(-758.97, -84.5) * mm, "end": v(-103.13, 25.5) * mm});
            skSolve(sketch);
        }
        {
            var Q0;
            Q0=qSketchRegion(id+"F33",true);
            extrude(context, id + "F34", {"entities" : qUnion([Q0]), "depth" : 240 * mm});
        }
        {
            var Q0;
            Q0=makeQuery(id+"F34.opExtrude","CAP_FACE",FACE,{"disambiguationData":[OSD([sQuery(id+"F33.wireOp",EDGE,"E264"),sQuery(id+"F33.wireOp",EDGE,"E265"),sQuery(id+"F33.wireOp",EDGE,"E266"),sQuery(id+"F33.wireOp",EDGE,"E267")])],"isStart":false});
            var sketch = newSketch(context, id + "F35", { "sketchPlane" : qUnion([Q0])});
            skLineSegment(sketch, "E268", {"start": v(-103.13, -334.5) * mm, "end": v(-103.13, 25.5) * mm});
            skLineSegment(sketch, "E269", {"start": v(-103.13, 25.5) * mm, "end": v(-263.89, -1.46) * mm});
            skLineSegment(sketch, "E270", {"start": v(-263.89, -1.46) * mm, "end": v(-263.89, -334.5) * mm});
            skLineSegment(sketch, "E271", {"start": v(-263.89, -334.5) * mm, "end": v(-103.13, -334.5) * mm});
            skSolve(sketch);
        }
        {
            var Q0;
            Q0=qSketchRegion(id+"F35",true);
            extrude(context, id + "F36", {"entities" : qUnion([Q0]), "operationType" : NewBodyOperationType.ADD, "depth" : 145 * mm});
        }
        {
            var Q0;
            Q0=makeQuery(id+"F36.boolean.opBoolean","MERGE",FACE,{"derivedFrom":[makeQuery(id+"F34.opExtrude","SWEPT_FACE",FACE,{"disambiguationData":[OSD([sQuery(id+"F33.wireOp",EDGE,"E267")])]}),makeQuery(id+"F36.opExtrude","SWEPT_FACE",FACE,{"disambiguationData":[OSD([sQuery(id+"F35.wireOp",EDGE,"E269")])]})]});
            var sketch = newSketch(context, id + "F37", { "sketchPlane" : qUnion([Q0])});
            skLineSegment(sketch, "E272", {"start": v(-187.5, -102.5) * mm, "end": v(187.5, -102.5) * mm});
            skLineSegment(sketch, "E273", {"start": v(187.5, -102.5) * mm, "end": v(187.5, -255.5) * mm});
            skLineSegment(sketch, "E274", {"start": v(187.5, -255.5) * mm, "end": v(42.5, -255.5) * mm});
            skLineSegment(sketch, "E275", {"start": v(42.5, -255.5) * mm, "end": v(42.5, -757.5) * mm});
            skLineSegment(sketch, "E276", {"start": v(42.5, -757.5) * mm, "end": v(-187.5, -757.5) * mm});
            skLineSegment(sketch, "E277", {"start": v(-187.5, -757.5) * mm, "end": v(-187.5, -102.5) * mm});
            skSolve(sketch);
        }
        {
            var Q0;
            Q0=qSketchRegion(id+"F37",true);
            extrude(context, id + "F38", {"entities" : qUnion([Q0]), "operationType" : NewBodyOperationType.REMOVE, "oppositeDirection" : true, "depth" : 5 * mm});
        }
        {
            var Q0;
            Q0=qSketchRegion(id+"F29",true);
            extrude(context, id + "F39", {"entities" : qUnion([Q0]), "oppositeDirection" : true, "depth" : 25 * mm});
        }
        {
            var Q0;
            Q0=makeQuery(id+"F2.imprint","IMPRINT",FACE,{"disambiguationData":[TD([[makeQuery(id+"F2.imprint","IMPRINT",EDGE,{"derivedFrom":sQuery(id+"F2.wireOp",EDGE,"E21")}),-1.0]])]});
            var sketch = newSketch(context, id + "F40", { "sketchPlane" : qUnion([Q0])});
            skLineSegment(sketch, "E278", {"start": v(475, 325) * mm, "end": v(475, 290) * mm, "construction": true});
            skLineSegment(sketch, "E279", {"start": v(475, 290) * mm, "end": v(510, 290) * mm, "construction": true});
            skLineSegment(sketch, "E280", {"start": v(475, 290) * mm, "end": v(502.9, 317.9) * mm, "construction": true});
            skLineSegment(sketch, "E281", {"start": v(471.82, 297.42) * mm, "end": v(482.42, 286.82) * mm});
            skLineSegment(sketch, "E282", {"start": v(489.5, 286.82) * mm, "end": v(496.57, 293.89) * mm});
            skLineSegment(sketch, "E283", {"start": v(496.57, 293.89) * mm, "end": v(478.89, 311.57) * mm});
            skLineSegment(sketch, "E284", {"start": v(478.89, 311.57) * mm, "end": v(471.82, 304.5) * mm});
            skPoint(sketch, "E285.visualSharp", {"position": v(468.28, 300.96) * mm});
            skArc(sketch, "E285.filletArc", {"start": v(471.82, 304.5) * mm, "mid": v(470.35, 300.96) * mm, "end": v(471.82, 297.42) * mm});
            skPoint(sketch, "E286.visualSharp", {"position": v(485.96, 283.28) * mm});
            skArc(sketch, "E286.filletArc", {"start": v(482.42, 286.82) * mm, "mid": v(485.96, 285.35) * mm, "end": v(489.5, 286.82) * mm});
            skLineSegment(sketch, "E287", {"start": v(475, 237) * mm, "end": v(475, 202) * mm, "construction": true});
            skLineSegment(sketch, "E288", {"start": v(475, 202) * mm, "end": v(510, 202) * mm, "construction": true});
            skLineSegment(sketch, "E289", {"start": v(475, 202) * mm, "end": v(502.9, 229.9) * mm, "construction": true});
            skLineSegment(sketch, "E290", {"start": v(471.82, 209.42) * mm, "end": v(482.42, 198.82) * mm});
            skLineSegment(sketch, "E291", {"start": v(489.5, 198.82) * mm, "end": v(496.57, 205.89) * mm});
            skLineSegment(sketch, "E292", {"start": v(496.57, 205.89) * mm, "end": v(478.89, 223.57) * mm});
            skLineSegment(sketch, "E293", {"start": v(478.89, 223.57) * mm, "end": v(471.82, 216.5) * mm});
            skPoint(sketch, "E294.visualSharp", {"position": v(468.28, 212.96) * mm});
            skArc(sketch, "E294.filletArc", {"start": v(471.82, 216.5) * mm, "mid": v(470.35, 212.96) * mm, "end": v(471.82, 209.42) * mm});
            skPoint(sketch, "E295.visualSharp", {"position": v(485.96, 195.28) * mm});
            skArc(sketch, "E295.filletArc", {"start": v(482.42, 198.82) * mm, "mid": v(485.96, 197.35) * mm, "end": v(489.5, 198.82) * mm});
            skLineSegment(sketch, "E296", {"start": v(475, 149) * mm, "end": v(475, 114) * mm, "construction": true});
            skLineSegment(sketch, "E297", {"start": v(475, 114) * mm, "end": v(510, 114) * mm, "construction": true});
            skLineSegment(sketch, "E298", {"start": v(475, 114) * mm, "end": v(502.9, 141.9) * mm, "construction": true});
            skLineSegment(sketch, "E299", {"start": v(471.82, 121.42) * mm, "end": v(482.42, 110.82) * mm});
            skLineSegment(sketch, "E300", {"start": v(489.5, 110.82) * mm, "end": v(496.57, 117.89) * mm});
            skLineSegment(sketch, "E301", {"start": v(496.57, 117.89) * mm, "end": v(478.89, 135.57) * mm});
            skLineSegment(sketch, "E302", {"start": v(478.89, 135.57) * mm, "end": v(471.82, 128.5) * mm});
            skPoint(sketch, "E303.visualSharp", {"position": v(468.28, 124.96) * mm});
            skArc(sketch, "E303.filletArc", {"start": v(471.82, 128.5) * mm, "mid": v(470.35, 124.96) * mm, "end": v(471.82, 121.42) * mm});
            skArc(sketch, "E304.filletArc", {"start": v(482.42, 110.82) * mm, "mid": v(485.96, 109.35) * mm, "end": v(489.5, 110.82) * mm});
            skLineSegment(sketch, "E305.MirrorCS", {"start": v(475, 220.3) * mm, "end": v(502.9, 192.41) * mm, "construction": true});
            skLineSegment(sketch, "E306", {"start": v(502.5, 156.5) * mm, "end": v(517.5, 141.5) * mm, "construction": true});
            skLineSegment(sketch, "E307.MirrorCS", {"start": v(523.43, 180.11) * mm, "end": v(530.5, 187.18) * mm});
            skLineSegment(sketch, "E308.MirrorCS", {"start": v(537.58, 187.18) * mm, "end": v(548.18, 176.58) * mm});
            skLineSegment(sketch, "E309.MirrorCS", {"start": v(541.11, 162.43) * mm, "end": v(523.43, 180.11) * mm});
            skArc(sketch, "E310.MirrorCS", {"start": v(530.5, 187.18) * mm, "mid": v(534.04, 188.65) * mm, "end": v(537.58, 187.18) * mm});
            skLineSegment(sketch, "E311.MirrorCS", {"start": v(548.18, 169.5) * mm, "end": v(541.11, 162.43) * mm});
            skArc(sketch, "E312.MirrorCS", {"start": v(548.18, 176.58) * mm, "mid": v(549.65, 173.04) * mm, "end": v(548.18, 169.5) * mm});
            skLineSegment(sketch, "E313.MirrorCS", {"start": v(510, 184) * mm, "end": v(545, 184) * mm, "construction": true});
            skLineSegment(sketch, "E314.MirrorCS", {"start": v(545, 184) * mm, "end": v(545, 149) * mm, "construction": true});
            skLineSegment(sketch, "E315.MirrorCS", {"start": v(545, 184) * mm, "end": v(517.1, 156.1) * mm, "construction": true});
            skPoint(sketch, "E316.MirrorP", {"position": v(534.04, 190.72) * mm});
            skLineSegment(sketch, "E317", {"start": v(-335, 322) * mm, "end": v(-335, 287) * mm, "construction": true});
            skLineSegment(sketch, "E318", {"start": v(-335, 287) * mm, "end": v(-300, 287) * mm, "construction": true});
            skLineSegment(sketch, "E319", {"start": v(-335, 287) * mm, "end": v(-307.1, 314.9) * mm, "construction": true});
            skLineSegment(sketch, "E320", {"start": v(-338.18, 294.42) * mm, "end": v(-327.58, 283.82) * mm});
            skLineSegment(sketch, "E321", {"start": v(-320.5, 283.82) * mm, "end": v(-313.43, 290.89) * mm});
            skLineSegment(sketch, "E322", {"start": v(-313.43, 290.89) * mm, "end": v(-331.11, 308.57) * mm});
            skLineSegment(sketch, "E323", {"start": v(-331.11, 308.57) * mm, "end": v(-338.18, 301.5) * mm});
            skPoint(sketch, "E324.visualSharp", {"position": v(-341.72, 297.96) * mm});
            skArc(sketch, "E324.filletArc", {"start": v(-338.18, 301.5) * mm, "mid": v(-339.65, 297.96) * mm, "end": v(-338.18, 294.42) * mm});
            skPoint(sketch, "E325.visualSharp", {"position": v(-324.04, 280.28) * mm});
            skArc(sketch, "E325.filletArc", {"start": v(-327.58, 283.82) * mm, "mid": v(-324.04, 282.35) * mm, "end": v(-320.5, 283.82) * mm});
            skLineSegment(sketch, "E326", {"start": v(-335, 232) * mm, "end": v(-335, 197) * mm, "construction": true});
            skLineSegment(sketch, "E327", {"start": v(-335, 197) * mm, "end": v(-300, 197) * mm, "construction": true});
            skLineSegment(sketch, "E328", {"start": v(-335, 197) * mm, "end": v(-307.1, 224.9) * mm, "construction": true});
            skLineSegment(sketch, "E329", {"start": v(-338.18, 204.42) * mm, "end": v(-327.58, 193.82) * mm});
            skLineSegment(sketch, "E330", {"start": v(-320.5, 193.82) * mm, "end": v(-313.43, 200.89) * mm});
            skLineSegment(sketch, "E331", {"start": v(-313.43, 200.89) * mm, "end": v(-331.11, 218.57) * mm});
            skLineSegment(sketch, "E332", {"start": v(-331.11, 218.57) * mm, "end": v(-338.18, 211.5) * mm});
            skPoint(sketch, "E333.visualSharp", {"position": v(-341.72, 207.96) * mm});
            skArc(sketch, "E333.filletArc", {"start": v(-338.18, 211.5) * mm, "mid": v(-339.65, 207.96) * mm, "end": v(-338.18, 204.42) * mm});
            skPoint(sketch, "E334.visualSharp", {"position": v(-324.04, 190.28) * mm});
            skArc(sketch, "E334.filletArc", {"start": v(-327.58, 193.82) * mm, "mid": v(-324.04, 192.35) * mm, "end": v(-320.5, 193.82) * mm});
            skLineSegment(sketch, "E335", {"start": v(-545, 210) * mm, "end": v(-545, 175) * mm, "construction": true});
            skLineSegment(sketch, "E336", {"start": v(-545, 175) * mm, "end": v(-510, 175) * mm, "construction": true});
            skLineSegment(sketch, "E337", {"start": v(-545, 175) * mm, "end": v(-517.1, 202.9) * mm, "construction": true});
            skLineSegment(sketch, "E338", {"start": v(-548.18, 182.42) * mm, "end": v(-537.58, 171.82) * mm});
            skLineSegment(sketch, "E339", {"start": v(-530.5, 171.82) * mm, "end": v(-523.43, 178.89) * mm});
            skLineSegment(sketch, "E340", {"start": v(-523.43, 178.89) * mm, "end": v(-541.11, 196.57) * mm});
            skLineSegment(sketch, "E341", {"start": v(-541.11, 196.57) * mm, "end": v(-548.18, 189.5) * mm});
            skPoint(sketch, "E342.visualSharp", {"position": v(-551.72, 185.96) * mm});
            skArc(sketch, "E342.filletArc", {"start": v(-548.18, 189.5) * mm, "mid": v(-549.65, 185.96) * mm, "end": v(-548.18, 182.42) * mm});
            skArc(sketch, "E343.filletArc", {"start": v(-537.58, 171.82) * mm, "mid": v(-534.04, 170.35) * mm, "end": v(-530.5, 171.82) * mm});
            skLineSegment(sketch, "E344", {"start": v(-517.24, 217.24) * mm, "end": v(-502.76, 202.76) * mm, "construction": true});
            skLineSegment(sketch, "E345.MirrorCS", {"start": v(-478.89, 223.43) * mm, "end": v(-496.57, 241.11) * mm});
            skLineSegment(sketch, "E346.MirrorCS", {"start": v(-496.57, 241.11) * mm, "end": v(-489.5, 248.18) * mm});
            skArc(sketch, "E347.MirrorCS", {"start": v(-471.82, 237.58) * mm, "mid": v(-470.35, 234.04) * mm, "end": v(-471.82, 230.5) * mm});
            skLineSegment(sketch, "E348.MirrorCS", {"start": v(-475, 245) * mm, "end": v(-475, 210) * mm, "construction": true});
            skLineSegment(sketch, "E349.MirrorCS", {"start": v(-510, 245) * mm, "end": v(-475, 245) * mm, "construction": true});
            skLineSegment(sketch, "E350.MirrorCS", {"start": v(-475, 245) * mm, "end": v(-502.9, 217.1) * mm, "construction": true});
            skArc(sketch, "E351.MirrorCS", {"start": v(-489.5, 248.18) * mm, "mid": v(-485.96, 249.65) * mm, "end": v(-482.42, 248.18) * mm});
            skLineSegment(sketch, "E352.MirrorCS", {"start": v(-471.82, 230.5) * mm, "end": v(-478.89, 223.43) * mm});
            skPoint(sketch, "E353.MirrorP", {"position": v(-485.96, 251.72) * mm});
            skLineSegment(sketch, "E354.MirrorCS", {"start": v(-482.42, 248.18) * mm, "end": v(-471.82, 237.58) * mm});
            skSolve(sketch);
        }
        {
            var Q0;
            Q0=qSketchRegion(id+"F40",true);
            extrude(context, id + "F41", {"entities" : qUnion([Q0]), "operationType" : NewBodyOperationType.REMOVE, "oppositeDirection" : true, "depth" : 3 * mm});
        }
        {
            var Q0;
            Q0=makeQuery(id+"F2.imprint","IMPRINT",FACE,{"disambiguationData":[TD([[makeQuery(id+"F2.imprint","IMPRINT",EDGE,{"derivedFrom":sQuery(id+"F2.wireOp",EDGE,"E21")}),-1.0]])]});
            var sketch = newSketch(context, id + "F42", { "sketchPlane" : qUnion([Q0])});
            skLineSegment(sketch, "E355.top", {"start": v(-188, 2) * mm, "end": v(-28, 2) * mm});
            skLineSegment(sketch, "E355.left", {"start": v(-220, 129.04) * mm, "end": v(-220, 60.77) * mm});
            skLineSegment(sketch, "E355.right", {"start": v(-25, 129.04) * mm, "end": v(-25, 5) * mm});
            skLineSegment(sketch, "E356", {"start": v(-208.75, 46.67) * mm, "end": v(-190.77, 3.84) * mm});
            skLineSegment(sketch, "E357", {"start": v(-155, 142) * mm, "end": v(-90, 142) * mm});
            skLineSegment(sketch, "E358", {"start": v(-90, 142) * mm, "end": v(-27.53, 132) * mm});
            skLineSegment(sketch, "E359", {"start": v(-155, 142) * mm, "end": v(-217.47, 132) * mm});
            skPoint(sketch, "E360.visualSharp", {"position": v(-220, 131.6) * mm});
            skArc(sketch, "E360.filletArc", {"start": v(-217.47, 132) * mm, "mid": v(-219.28, 130.98) * mm, "end": v(-220, 129.04) * mm});
            skPoint(sketch, "E361.visualSharp", {"position": v(-25, 131.6) * mm});
            skArc(sketch, "E361.filletArc", {"start": v(-25, 129.04) * mm, "mid": v(-25.72, 130.98) * mm, "end": v(-27.53, 132) * mm});
            skPoint(sketch, "E362.visualSharp", {"position": v(-25, 2) * mm});
            skArc(sketch, "E362.filletArc", {"start": v(-28, 2) * mm, "mid": v(-25.88, 2.88) * mm, "end": v(-25, 5) * mm});
            skPoint(sketch, "E363.visualSharp", {"position": v(-190, 2) * mm});
            skArc(sketch, "E363.filletArc", {"start": v(-190.77, 3.84) * mm, "mid": v(-189.66, 2.5) * mm, "end": v(-188, 2) * mm});
            skArc(sketch, "E364", {"start": v(-208.75, 46.67) * mm, "mid": v(-212.77, 53.21) * mm, "end": v(-218.59, 58.22) * mm});
            skPoint(sketch, "E365.visualSharp", {"position": v(-220, 59.04) * mm});
            skArc(sketch, "E365.filletArc", {"start": v(-220, 60.77) * mm, "mid": v(-219.62, 59.31) * mm, "end": v(-218.59, 58.22) * mm});
            skSolve(sketch);
        }
        {
            var Q0;
            Q0=qSketchRegion(id+"F42",true);
            extrude(context, id + "F43", {"entities" : qUnion([Q0]), "depth" : 10 * mm});
        }
        {
            var Q0;
            Q0=makeQuery(id+"F2.imprint","IMPRINT",FACE,{"disambiguationData":[TD([[makeQuery(id+"F2.imprint","IMPRINT",EDGE,{"derivedFrom":sQuery(id+"F2.wireOp",EDGE,"E21")}),-1.0]])]});
            var sketch = newSketch(context, id + "F44", { "sketchPlane" : qUnion([Q0])});
            skLineSegment(sketch, "E366.bottom", {"start": v(-220, 129.04) * mm, "end": v(-226, 129.04) * mm});
            skLineSegment(sketch, "E366.top", {"start": v(-220, 60.77) * mm, "end": v(-226, 60.77) * mm});
            skLineSegment(sketch, "E366.left", {"start": v(-220, 129.04) * mm, "end": v(-220, 60.77) * mm});
            skLineSegment(sketch, "E366.right", {"start": v(-226, 129.04) * mm, "end": v(-226, 60.77) * mm});
            skLineSegment(sketch, "E367.bottom", {"start": v(-25, 129.04) * mm, "end": v(-19, 129.04) * mm});
            skLineSegment(sketch, "E367.top", {"start": v(-25, 5) * mm, "end": v(-19, 5) * mm});
            skLineSegment(sketch, "E367.left", {"start": v(-25, 129.04) * mm, "end": v(-25, 5) * mm});
            skLineSegment(sketch, "E367.right", {"start": v(-19, 129.04) * mm, "end": v(-19, 5) * mm});
            skCircle(sketch, "E368", {"center": v(-223, 119.04) * mm, "radius": 1.5 * mm});
            skCircle(sketch, "E369", {"center": v(-223, 70.77) * mm, "radius": 1.5 * mm});
            skCircle(sketch, "E370", {"center": v(-22, 119.04) * mm, "radius": 1.5 * mm});
            skCircle(sketch, "E371", {"center": v(-22, 67.04) * mm, "radius": 1.5 * mm});
            skCircle(sketch, "E372", {"center": v(-22, 15) * mm, "radius": 1.5 * mm});
            skSolve(sketch);
        }
        {
            var Q0;
            Q0=makeQuery(id+"F43.opExtrude","CAP_EDGE",EDGE,{"disambiguationData":[OSD([sQuery(id+"F42.wireOp",EDGE,"E359")])],"isStart":false});
            var Q1;
            Q1=makeQuery(id+"F43.opExtrude","CAP_EDGE",EDGE,{"disambiguationData":[OSD([sQuery(id+"F42.wireOp",EDGE,"E357")])],"isStart":false});
            var Q2;
            Q2=makeQuery(id+"F43.opExtrude","CAP_EDGE",EDGE,{"disambiguationData":[OSD([sQuery(id+"F42.wireOp",EDGE,"E358")])],"isStart":false});
            var Q3;
            Q3=makeQuery(id+"F43.opExtrude","CAP_EDGE",EDGE,{"disambiguationData":[OSD([sQuery(id+"F42.wireOp",EDGE,"uBvkl1DK-ICnH-D8pt-GGez-HArn9p07z3o4")])],"isStart":false});
            var Q4;
            Q4=makeQuery(id+"F43.opExtrude","CAP_EDGE",EDGE,{"disambiguationData":[OSD([sQuery(id+"F42.wireOp",EDGE,"E356")])],"isStart":false});
            fillet(context, id + "F45", {"entities" : qUnion([Q0, Q1, Q2, Q3, Q4]), "radius" : 2 * mm, "tangentPropagation" : true, "allowEdgeOverflow" : false});
        }
        {
            var Q0;
            Q0=makeQuery(id+"F43.opExtrude","CAP_FACE",FACE,{"disambiguationData":[OSD([sQuery(id+"F42.wireOp",EDGE,"E355.top"),sQuery(id+"F42.wireOp",EDGE,"E355.left"),sQuery(id+"F42.wireOp",EDGE,"E355.right"),sQuery(id+"F42.wireOp",EDGE,"uBvkl1DK-ICnH-D8pt-GGez-HArn9p07z3o4"),sQuery(id+"F42.wireOp",EDGE,"E356"),sQuery(id+"F42.wireOp",EDGE,"sZQz9iDY-4fOH-cXF0-kQPg-hJRuD6cjQATF"),sQuery(id+"F42.wireOp",EDGE,"d80992fc-50c1-48bc-b6fb-9e52991e1214.filletArc"),sQuery(id+"F42.wireOp",EDGE,"E357"),sQuery(id+"F42.wireOp",EDGE,"E358"),sQuery(id+"F42.wireOp",EDGE,"E359"),sQuery(id+"F42.wireOp",EDGE,"E360.filletArc"),sQuery(id+"F42.wireOp",EDGE,"E361.filletArc"),sQuery(id+"F42.wireOp",EDGE,"E362.filletArc")])],"isStart":false});
            var sketch = newSketch(context, id + "F46", { "sketchPlane" : qUnion([Q0])});
            skCircle(sketch, "E373", {"center": v(-195, 114) * mm, "radius": 9 * mm});
            skCircle(sketch, "E374", {"center": v(-168, 114) * mm, "radius": 9 * mm});
            skCircle(sketch, "E375", {"center": v(-137.5, 114) * mm, "radius": 9 * mm});
            skCircle(sketch, "E376", {"center": v(-107.5, 114) * mm, "radius": 9 * mm});
            skCircle(sketch, "E377", {"center": v(-77, 114) * mm, "radius": 9 * mm});
            skCircle(sketch, "E378", {"center": v(-50, 114) * mm, "radius": 9 * mm});
            skCircle(sketch, "E379", {"center": v(-168, 84) * mm, "radius": 9 * mm});
            skCircle(sketch, "E380", {"center": v(-137.5, 84) * mm, "radius": 9 * mm});
            skCircle(sketch, "E381", {"center": v(-107.5, 84) * mm, "radius": 9 * mm});
            skCircle(sketch, "E382", {"center": v(-77, 84) * mm, "radius": 7.5 * mm});
            skCircle(sketch, "E383", {"center": v(-50, 84) * mm, "radius": 9 * mm});
            skCircle(sketch, "E384", {"center": v(-50, 54) * mm, "radius": 9 * mm});
            skCircle(sketch, "E385", {"center": v(-50, 27) * mm, "radius": 7.5 * mm});
            skCircle(sketch, "E386", {"center": v(-122.5, 49) * mm, "radius": 7.5 * mm});
            skLineSegment(sketch, "E387.bottom", {"start": v(-100.16, 54) * mm, "end": v(-85.16, 54) * mm});
            skLineSegment(sketch, "E387.top", {"start": v(-100.16, 29) * mm, "end": v(-85.16, 29) * mm});
            skLineSegment(sketch, "E387.left", {"start": v(-100.16, 54) * mm, "end": v(-100.16, 29) * mm});
            skLineSegment(sketch, "E387.right", {"start": v(-85.16, 54) * mm, "end": v(-85.16, 29) * mm});
            skSolve(sketch);
        }
        {
            var Q0;
            Q0=makeQuery(id+"F43.opExtrude","CAP_FACE",FACE,{"disambiguationData":[OSD([sQuery(id+"F42.wireOp",EDGE,"E355.top"),sQuery(id+"F42.wireOp",EDGE,"E355.left"),sQuery(id+"F42.wireOp",EDGE,"E355.right"),sQuery(id+"F42.wireOp",EDGE,"E356"),sQuery(id+"F42.wireOp",EDGE,"E357"),sQuery(id+"F42.wireOp",EDGE,"E358"),sQuery(id+"F42.wireOp",EDGE,"E359"),sQuery(id+"F42.wireOp",EDGE,"E360.filletArc"),sQuery(id+"F42.wireOp",EDGE,"E361.filletArc"),sQuery(id+"F42.wireOp",EDGE,"E362.filletArc"),sQuery(id+"F42.wireOp",EDGE,"E363.filletArc"),sQuery(id+"F42.wireOp",EDGE,"E364"),sQuery(id+"F42.wireOp",EDGE,"E365.filletArc")])],"isStart":true});
            shell(context, id + "F47", {"entities" : qUnion([Q0]), "thickness" : 2 * mm});
        }
        {
            var Q0;
            Q0=qSketchRegion(id+"F46",true);
            extrude(context, id + "F48", {"entities" : qUnion([Q0]), "operationType" : NewBodyOperationType.REMOVE, "oppositeDirection" : true, "depth" : 3 * mm});
        }
        {
            var Q0;
            Q0=qSketchRegion(id+"F44",true);
            extrude(context, id + "F49", {"entities" : qUnion([Q0]), "operationType" : NewBodyOperationType.ADD, "depth" : 2 * mm});
        }
    });
